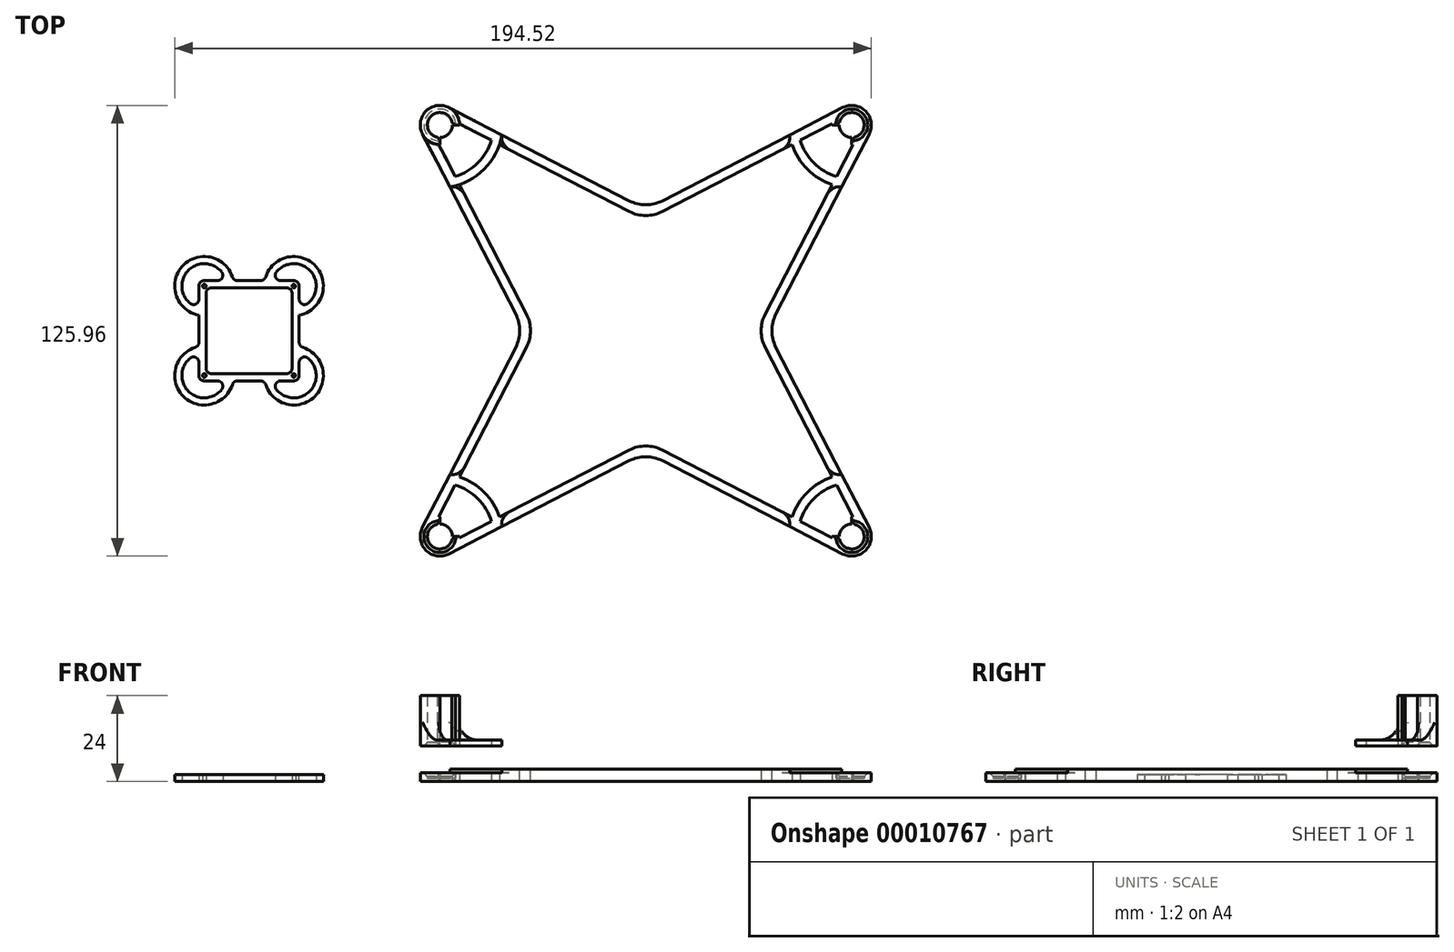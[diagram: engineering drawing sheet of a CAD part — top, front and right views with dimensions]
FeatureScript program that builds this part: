
annotation { "Feature Type Name" : "Feature", "Feature Type Description" : "" }
export const myFeature = defineFeature(function(context is Context, id is Id, definition is map)
    precondition{}
    {
        {
            var Q0;
            Q0=qCreatedBy(makeId("Top.planeOp"),FACE);
            var sketch = newSketch(context, id + "F0", { "sketchPlane" : qUnion([Q0])});
            skLineSegment(sketch, "E0.rect.bottom", {"start": v(57.5, 57.5) * mm, "end": v(-57.5, 57.5) * mm});
            skLineSegment(sketch, "E0.rect.top", {"start": v(57.5, -57.5) * mm, "end": v(-57.5, -57.5) * mm});
            skLineSegment(sketch, "E0.rect.left", {"start": v(57.5, 57.5) * mm, "end": v(57.5, -57.5) * mm});
            skLineSegment(sketch, "E0.rect.right", {"start": v(-57.5, 57.5) * mm, "end": v(-57.5, -57.5) * mm});
            skPoint(sketch, "E0.rect.middle", {"position": v(0, 0) * mm});
            skLineSegment(sketch, "E1", {"start": v(0, 33.94) * mm, "end": v(-33.94, 0) * mm});
            skLineSegment(sketch, "E2", {"start": v(-33.94, 0) * mm, "end": v(0, -33.94) * mm});
            skLineSegment(sketch, "E3", {"start": v(0, -33.94) * mm, "end": v(33.94, 0) * mm});
            skLineSegment(sketch, "E4", {"start": v(33.94, 0) * mm, "end": v(0, 33.94) * mm});
            skCircle(sketch, "E5", {"center": v(57.5, 57.5) * mm, "radius": 3.48 * mm});
            skCircle(sketch, "E6", {"center": v(57.5, 57.5) * mm, "radius": 5.47 * mm});
            skLineSegment(sketch, "E7", {"start": v(57.5, 60.98) * mm, "end": v(57.5, 62.98) * mm, "construction": true});
            skCircle(sketch, "E8", {"center": v(-57.5, 57.5) * mm, "radius": 3.48 * mm});
            skCircle(sketch, "E9", {"center": v(-57.5, 57.5) * mm, "radius": 5.47 * mm});
            skCircle(sketch, "E10", {"center": v(-57.5, -57.5) * mm, "radius": 3.48 * mm});
            skCircle(sketch, "E11", {"center": v(-57.5, -57.5) * mm, "radius": 5.47 * mm});
            skCircle(sketch, "E12", {"center": v(57.5, -57.5) * mm, "radius": 3.48 * mm});
            skCircle(sketch, "E13", {"center": v(57.5, -57.5) * mm, "radius": 5.47 * mm});
            skLineSegment(sketch, "E14", {"start": v(62.36, 54.99) * mm, "end": v(33.94, 0) * mm});
            skLineSegment(sketch, "E15", {"start": v(33.94, 0) * mm, "end": v(62.36, -54.99) * mm});
            skLineSegment(sketch, "E16", {"start": v(54.99, -62.36) * mm, "end": v(0, -33.94) * mm});
            skLineSegment(sketch, "E17", {"start": v(0, -33.94) * mm, "end": v(-54.99, -62.36) * mm});
            skLineSegment(sketch, "E18", {"start": v(-62.36, -54.99) * mm, "end": v(-33.94, 0) * mm});
            skLineSegment(sketch, "E19", {"start": v(-33.94, 0) * mm, "end": v(-62.36, 54.99) * mm});
            skLineSegment(sketch, "E20", {"start": v(-54.99, 62.36) * mm, "end": v(0, 33.94) * mm});
            skLineSegment(sketch, "E21", {"start": v(0, 33.94) * mm, "end": v(54.99, 62.36) * mm});
            skLineSegment(sketch, "E22.0", {"start": v(30.94, 0) * mm, "end": v(0, 30.94) * mm});
            skLineSegment(sketch, "E22.1", {"start": v(0, -30.94) * mm, "end": v(30.94, 0) * mm});
            skLineSegment(sketch, "E22.2", {"start": v(-30.94, 0) * mm, "end": v(0, -30.94) * mm});
            skLineSegment(sketch, "E22.3", {"start": v(0, 30.94) * mm, "end": v(-30.94, 0) * mm});
            skLineSegment(sketch, "E23", {"start": v(-30.94, 0) * mm, "end": v(-57.84, 52.04) * mm});
            skLineSegment(sketch, "E24", {"start": v(-30.94, 0) * mm, "end": v(-57.84, -52.04) * mm});
            skLineSegment(sketch, "E25", {"start": v(30.94, 0) * mm, "end": v(33.94, 0) * mm, "construction": true});
            skLineSegment(sketch, "E26", {"start": v(0, -30.94) * mm, "end": v(-52.04, -57.84) * mm});
            skLineSegment(sketch, "E27", {"start": v(0, -30.94) * mm, "end": v(52.04, -57.84) * mm});
            skLineSegment(sketch, "E28", {"start": v(57.84, -52.04) * mm, "end": v(30.94, 0) * mm});
            skLineSegment(sketch, "E29", {"start": v(30.94, 0) * mm, "end": v(57.84, 52.04) * mm});
            skLineSegment(sketch, "E30", {"start": v(52.04, 57.84) * mm, "end": v(0, 30.94) * mm});
            skLineSegment(sketch, "E31", {"start": v(0, 30.94) * mm, "end": v(-52.04, 57.84) * mm});
            skCircle(sketch, "E32", {"center": v(57.5, 57.5) * mm, "radius": 15 * mm});
            skCircle(sketch, "E33", {"center": v(57.5, 57.5) * mm, "radius": 17.5 * mm});
            skLineSegment(sketch, "E34", {"start": v(57.5, 72.5) * mm, "end": v(57.5, 75) * mm, "construction": true});
            skCircle(sketch, "E35", {"center": v(-57.5, 57.5) * mm, "radius": 15 * mm});
            skCircle(sketch, "E36", {"center": v(-57.5, 57.5) * mm, "radius": 17.5 * mm});
            skCircle(sketch, "E37", {"center": v(-57.5, -57.5) * mm, "radius": 15 * mm});
            skCircle(sketch, "E38", {"center": v(-57.5, -57.5) * mm, "radius": 17.5 * mm});
            skCircle(sketch, "E39", {"center": v(57.5, -57.5) * mm, "radius": 15 * mm});
            skCircle(sketch, "E40", {"center": v(57.5, -57.5) * mm, "radius": 17.5 * mm});
            skLineSegment(sketch, "E41.rect.bottom", {"start": v(-98.29, 12.5) * mm, "end": v(-123.29, 12.5) * mm, "construction": true});
            skLineSegment(sketch, "E41.rect.top", {"start": v(-98.29, -12.5) * mm, "end": v(-123.29, -12.5) * mm, "construction": true});
            skLineSegment(sketch, "E41.rect.left", {"start": v(-98.29, 12.5) * mm, "end": v(-98.29, -12.5) * mm, "construction": true});
            skLineSegment(sketch, "E41.rect.right", {"start": v(-123.29, 12.5) * mm, "end": v(-123.29, -12.5) * mm, "construction": true});
            skPoint(sketch, "E41.rect.middle", {"position": v(-110.79, 0) * mm});
            skCircle(sketch, "E42", {"center": v(-98.29, 12.5) * mm, "radius": 0.5 * mm});
            skCircle(sketch, "E43", {"center": v(-98.29, -12.5) * mm, "radius": 0.5 * mm});
            skCircle(sketch, "E44", {"center": v(-123.29, -12.5) * mm, "radius": 0.5 * mm});
            skCircle(sketch, "E45", {"center": v(-123.29, 12.5) * mm, "radius": 0.5 * mm});
            skCircle(sketch, "E46", {"center": v(-98.29, 12.5) * mm, "radius": 6.25 * mm});
            skCircle(sketch, "E47", {"center": v(-123.29, 12.5) * mm, "radius": 6.25 * mm});
            skCircle(sketch, "E48", {"center": v(-123.29, -12.5) * mm, "radius": 6.25 * mm});
            skCircle(sketch, "E49", {"center": v(-98.29, -12.5) * mm, "radius": 6.25 * mm});
            skCircle(sketch, "E50", {"center": v(-98.29, 12.5) * mm, "radius": 8.25 * mm});
            skLineSegment(sketch, "E51", {"start": v(-98.29, 18.75) * mm, "end": v(-98.29, 20.75) * mm, "construction": true});
            skCircle(sketch, "E52", {"center": v(-123.29, 12.5) * mm, "radius": 8.25 * mm});
            skCircle(sketch, "E53", {"center": v(-123.29, -12.5) * mm, "radius": 8.25 * mm});
            skCircle(sketch, "E54", {"center": v(-98.29, -12.5) * mm, "radius": 8.25 * mm});
            skLineSegment(sketch, "E55.rect.bottom", {"start": v(-96.79, 14) * mm, "end": v(-124.79, 14) * mm});
            skLineSegment(sketch, "E55.rect.top", {"start": v(-96.79, -14) * mm, "end": v(-124.79, -14) * mm});
            skLineSegment(sketch, "E55.rect.left", {"start": v(-96.79, 14) * mm, "end": v(-96.79, -14) * mm});
            skLineSegment(sketch, "E55.rect.right", {"start": v(-124.79, 14) * mm, "end": v(-124.79, -14) * mm});
            skLineSegment(sketch, "E56.rect.bottom", {"start": v(-98.79, 12) * mm, "end": v(-122.79, 12) * mm});
            skLineSegment(sketch, "E56.rect.top", {"start": v(-98.79, -12) * mm, "end": v(-122.79, -12) * mm});
            skLineSegment(sketch, "E56.rect.left", {"start": v(-98.79, 12) * mm, "end": v(-98.79, -12) * mm});
            skLineSegment(sketch, "E56.rect.right", {"start": v(-122.79, 12) * mm, "end": v(-122.79, -12) * mm});
            skLineSegment(sketch, "E57", {"start": v(-110.79, 12.5) * mm, "end": v(-110.79, 14) * mm, "construction": true});
            skLineSegment(sketch, "E58", {"start": v(-110.79, 12.5) * mm, "end": v(-110.79, 12) * mm, "construction": true});
            skCircle(sketch, "E59.cCircle", {"center": v(-110.79, 0) * mm, "radius": 17.68 * mm, "construction": true});
            skLineSegment(sketch, "E59.0", {"start": v(-110.79, 25) * mm, "end": v(-85.79, 0) * mm});
            skLineSegment(sketch, "E59.1", {"start": v(-85.79, 0) * mm, "end": v(-110.79, -25) * mm});
            skLineSegment(sketch, "E59.2", {"start": v(-110.79, -25) * mm, "end": v(-135.79, 0) * mm});
            skLineSegment(sketch, "E59.3", {"start": v(-135.79, 0) * mm, "end": v(-110.79, 25) * mm});
            skLineSegment(sketch, "E60", {"start": v(-124.79, 14) * mm, "end": v(-124.79, 20.61) * mm});
            skLineSegment(sketch, "E61", {"start": v(-122.79, 14) * mm, "end": v(-122.79, 20.73) * mm});
            skLineSegment(sketch, "E62", {"start": v(-98.79, 14) * mm, "end": v(-98.79, 20.73) * mm});
            skLineSegment(sketch, "E63", {"start": v(-96.79, 14) * mm, "end": v(-96.79, 20.61) * mm});
            skLineSegment(sketch, "E64", {"start": v(-124.79, -14) * mm, "end": v(-124.79, -20.61) * mm});
            skLineSegment(sketch, "E65", {"start": v(-122.79, -14) * mm, "end": v(-122.79, -20.73) * mm});
            skLineSegment(sketch, "E66", {"start": v(-98.79, -14) * mm, "end": v(-98.79, -20.73) * mm});
            skLineSegment(sketch, "E67", {"start": v(-96.79, -14) * mm, "end": v(-96.79, -20.61) * mm});
            skSolve(sketch);
        }
        {
            var Q0;
            {var subQ0=sQuery(id+"F0.wireOp",EDGE,"E9");var subQ7=sQuery(id+"F0.wireOp",EDGE,"E0.rect.bottom");var subQ8=makeQuery(id+"F0.imprint","INTERSECT",VERTEX,{"derivedFrom":[subQ7,subQ0]});Q0=makeQuery(id+"F0.imprint","IMPRINT",FACE,{"disambiguationData":[TD([[makeQuery(id+"F0.imprint","IMPRINT",EDGE,{"disambiguationData":[TD([[subQ8,-1.0]])],"derivedFrom":subQ7}),-1.0]])]});}
            var Q1;
            {var subQ1=sQuery(id+"F0.wireOp",EDGE,"E0.rect.right");var subQ5=sQuery(id+"F0.wireOp",EDGE,"E23");var subQ6=makeQuery(id+"F0.imprint","INTERSECT",VERTEX,{"derivedFrom":[subQ1,subQ5]});Q1=makeQuery(id+"F0.imprint","IMPRINT",FACE,{"disambiguationData":[TD([[makeQuery(id+"F0.imprint","IMPRINT",EDGE,{"disambiguationData":[TD([[subQ6,-1.0]])],"derivedFrom":subQ1}),-1.0]])]});}
            var Q2;
            {var subQ1=sQuery(id+"F0.wireOp",EDGE,"E23");var subQ5=sQuery(id+"F0.wireOp",EDGE,"E0.rect.right");var subQ6=makeQuery(id+"F0.imprint","INTERSECT",VERTEX,{"derivedFrom":[subQ5,subQ1]});Q2=makeQuery(id+"F0.imprint","IMPRINT",FACE,{"disambiguationData":[TD([[makeQuery(id+"F0.imprint","IMPRINT",EDGE,{"disambiguationData":[TD([[subQ6,-1.0]])],"derivedFrom":subQ5}),1.0]])]});}
            var Q3;
            {var subQ1=sQuery(id+"F0.wireOp",EDGE,"E0.rect.bottom");var subQ5=sQuery(id+"F0.wireOp",EDGE,"E20");var subQ6=makeQuery(id+"F0.imprint","INTERSECT",VERTEX,{"derivedFrom":[subQ1,subQ5]});Q3=makeQuery(id+"F0.imprint","IMPRINT",FACE,{"disambiguationData":[TD([[makeQuery(id+"F0.imprint","IMPRINT",EDGE,{"disambiguationData":[TD([[subQ6,-1.0]])],"derivedFrom":subQ1}),-1.0]])]});}
            var Q4;
            {var subQ3=sQuery(id+"F0.wireOp",EDGE,"E20");var subQ5=sQuery(id+"F0.wireOp",EDGE,"E0.rect.bottom");var subQ7=makeQuery(id+"F0.imprint","INTERSECT",VERTEX,{"derivedFrom":[subQ5,subQ3]});Q4=makeQuery(id+"F0.imprint","IMPRINT",FACE,{"disambiguationData":[TD([[makeQuery(id+"F0.imprint","IMPRINT",EDGE,{"disambiguationData":[TD([[subQ7,-1.0]])],"derivedFrom":subQ5}),1.0]])]});}
            var Q5;
            {var subQ0=sQuery(id+"F0.wireOp",EDGE,"E36");var subQ3=sQuery(id+"F0.wireOp",EDGE,"E19");var subQ4=makeQuery(id+"F0.imprint","INTERSECT",VERTEX,{"derivedFrom":[subQ3,subQ0]});Q5=makeQuery(id+"F0.imprint","IMPRINT",FACE,{"disambiguationData":[TD([[makeQuery(id+"F0.imprint","IMPRINT",EDGE,{"disambiguationData":[TD([[subQ4,-1.0]])],"derivedFrom":subQ3}),-1.0]])]});}
            var Q6;
            {var subQ3=sQuery(id+"F0.wireOp",EDGE,"E23");var subQ5=sQuery(id+"F0.wireOp",EDGE,"E36");var subQ7=makeQuery(id+"F0.imprint","INTERSECT",VERTEX,{"derivedFrom":[subQ3,subQ5]});Q6=makeQuery(id+"F0.imprint","IMPRINT",FACE,{"disambiguationData":[TD([[makeQuery(id+"F0.imprint","IMPRINT",EDGE,{"disambiguationData":[TD([[subQ7,-1.0]])],"derivedFrom":subQ3}),-1.0]])]});}
            var Q7;
            {var subQ3=sQuery(id+"F0.wireOp",EDGE,"E20");var subQ5=sQuery(id+"F0.wireOp",EDGE,"E35");var subQ7=makeQuery(id+"F0.imprint","INTERSECT",VERTEX,{"derivedFrom":[subQ3,subQ5]});Q7=makeQuery(id+"F0.imprint","IMPRINT",FACE,{"disambiguationData":[TD([[makeQuery(id+"F0.imprint","IMPRINT",EDGE,{"disambiguationData":[TD([[subQ7,-1.0]])],"derivedFrom":subQ3}),-1.0]])]});}
            extrude(context, id + "F1", {"entities" : qUnion([Q0, Q1, Q2, Q3, Q4, Q5, Q6, Q7]), "depth" : 1.6 * mm});
        }
        {
            var Q0;
            {var subQ0=sQuery(id+"F0.wireOp",EDGE,"E9");var subQ7=sQuery(id+"F0.wireOp",EDGE,"E0.rect.bottom");var subQ8=makeQuery(id+"F0.imprint","INTERSECT",VERTEX,{"derivedFrom":[subQ7,subQ0]});Q0=makeQuery(id+"F0.imprint","IMPRINT",FACE,{"disambiguationData":[TD([[makeQuery(id+"F0.imprint","IMPRINT",EDGE,{"disambiguationData":[TD([[subQ8,-1.0]])],"derivedFrom":subQ7}),-1.0]])]});}
            extrude(context, id + "F2", {"entities" : qUnion([Q0]), "operationType" : NewBodyOperationType.ADD, "depth" : 14 * mm});
        }
        {
            var Q0;
            {var subQ0=sQuery(id+"F0.wireOp",EDGE,"E9");Q0=makeQuery(id+"F2.boolean.opBoolean","INTERSECT",EDGE,{"disambiguationData":[OD(0.0)],"derivedFrom":[makeQuery(id+"F1.opExtrude","CAP_FACE",FACE,{"disambiguationData":[OSD([sQuery(id+"F0.wireOp",EDGE,"E0.rect.bottom"),sQuery(id+"F0.wireOp",EDGE,"E0.rect.right"),sQuery(id+"F0.wireOp",EDGE,"E8"),subQ0,sQuery(id+"F0.wireOp",EDGE,"E19"),sQuery(id+"F0.wireOp",EDGE,"E20"),sQuery(id+"F0.wireOp",EDGE,"E23"),sQuery(id+"F0.wireOp",EDGE,"E31"),sQuery(id+"F0.wireOp",EDGE,"E35"),sQuery(id+"F0.wireOp",EDGE,"E36")])],"isStart":false}),makeQuery(id+"F2.opExtrude","SWEPT_FACE",FACE,{"disambiguationData":[OSD([subQ0])]})]});}
            var Q1;
            {var subQ0=sQuery(id+"F0.wireOp",EDGE,"E9");Q1=makeQuery(id+"F2.boolean.opBoolean","INTERSECT",EDGE,{"disambiguationData":[OD(1.0)],"derivedFrom":[makeQuery(id+"F1.opExtrude","CAP_FACE",FACE,{"disambiguationData":[OSD([sQuery(id+"F0.wireOp",EDGE,"E0.rect.bottom"),sQuery(id+"F0.wireOp",EDGE,"E0.rect.right"),sQuery(id+"F0.wireOp",EDGE,"E8"),subQ0,sQuery(id+"F0.wireOp",EDGE,"E19"),sQuery(id+"F0.wireOp",EDGE,"E20"),sQuery(id+"F0.wireOp",EDGE,"E23"),sQuery(id+"F0.wireOp",EDGE,"E31"),sQuery(id+"F0.wireOp",EDGE,"E35"),sQuery(id+"F0.wireOp",EDGE,"E36")])],"isStart":false}),makeQuery(id+"F2.opExtrude","SWEPT_FACE",FACE,{"disambiguationData":[OSD([subQ0])]})]});}
            fillet(context, id + "F3", {"entities" : qUnion([Q0, Q1]), "radius" : 5 * mm, "tangentPropagation" : true, "allowEdgeOverflow" : false});
        }
        {
            var Q0;
            Q0=makeQuery(id+"F1.opExtrude","SWEPT_BODY",BODY,{"disambiguationData":[OSD([sQuery(id+"F0.wireOp",EDGE,"E0.rect.bottom"),sQuery(id+"F0.wireOp",EDGE,"E0.rect.right"),sQuery(id+"F0.wireOp",EDGE,"E8"),sQuery(id+"F0.wireOp",EDGE,"E9"),sQuery(id+"F0.wireOp",EDGE,"E19"),sQuery(id+"F0.wireOp",EDGE,"E20"),sQuery(id+"F0.wireOp",EDGE,"E23"),sQuery(id+"F0.wireOp",EDGE,"E31"),sQuery(id+"F0.wireOp",EDGE,"E35"),sQuery(id+"F0.wireOp",EDGE,"E36")])]});
            transform(context, id + "F4", {"entities" : qUnion([Q0]), "transformType" : TransformType.TRANSLATION_3D, "dx" : 0 * mm, "dy" : 0 * mm, "dz" : 10 * mm, "makeCopy" : false});
        }
        {
            var Q0;
            {var subQ1=sQuery(id+"F0.wireOp",EDGE,"E23");var subQ5=sQuery(id+"F0.wireOp",EDGE,"E0.rect.right");var subQ6=makeQuery(id+"F0.imprint","INTERSECT",VERTEX,{"derivedFrom":[subQ5,subQ1]});Q0=makeQuery(id+"F0.imprint","IMPRINT",FACE,{"disambiguationData":[TD([[makeQuery(id+"F0.imprint","IMPRINT",EDGE,{"disambiguationData":[TD([[subQ6,-1.0]])],"derivedFrom":subQ5}),1.0]])]});}
            var Q1;
            {var subQ1=sQuery(id+"F0.wireOp",EDGE,"E0.rect.right");var subQ5=sQuery(id+"F0.wireOp",EDGE,"E23");var subQ6=makeQuery(id+"F0.imprint","INTERSECT",VERTEX,{"derivedFrom":[subQ1,subQ5]});Q1=makeQuery(id+"F0.imprint","IMPRINT",FACE,{"disambiguationData":[TD([[makeQuery(id+"F0.imprint","IMPRINT",EDGE,{"disambiguationData":[TD([[subQ6,-1.0]])],"derivedFrom":subQ1}),-1.0]])]});}
            var Q2;
            {var subQ0=sQuery(id+"F0.wireOp",EDGE,"E9");var subQ7=sQuery(id+"F0.wireOp",EDGE,"E0.rect.bottom");var subQ8=makeQuery(id+"F0.imprint","INTERSECT",VERTEX,{"derivedFrom":[subQ7,subQ0]});Q2=makeQuery(id+"F0.imprint","IMPRINT",FACE,{"disambiguationData":[TD([[makeQuery(id+"F0.imprint","IMPRINT",EDGE,{"disambiguationData":[TD([[subQ8,-1.0]])],"derivedFrom":subQ7}),-1.0]])]});}
            var Q3;
            {var subQ1=sQuery(id+"F0.wireOp",EDGE,"E0.rect.bottom");var subQ5=sQuery(id+"F0.wireOp",EDGE,"E20");var subQ6=makeQuery(id+"F0.imprint","INTERSECT",VERTEX,{"derivedFrom":[subQ1,subQ5]});Q3=makeQuery(id+"F0.imprint","IMPRINT",FACE,{"disambiguationData":[TD([[makeQuery(id+"F0.imprint","IMPRINT",EDGE,{"disambiguationData":[TD([[subQ6,-1.0]])],"derivedFrom":subQ1}),-1.0]])]});}
            var Q4;
            {var subQ3=sQuery(id+"F0.wireOp",EDGE,"E20");var subQ5=sQuery(id+"F0.wireOp",EDGE,"E0.rect.bottom");var subQ7=makeQuery(id+"F0.imprint","INTERSECT",VERTEX,{"derivedFrom":[subQ5,subQ3]});Q4=makeQuery(id+"F0.imprint","IMPRINT",FACE,{"disambiguationData":[TD([[makeQuery(id+"F0.imprint","IMPRINT",EDGE,{"disambiguationData":[TD([[subQ7,-1.0]])],"derivedFrom":subQ5}),1.0]])]});}
            var Q5;
            {var subQ0=sQuery(id+"F0.wireOp",EDGE,"E36");var subQ3=sQuery(id+"F0.wireOp",EDGE,"E19");var subQ4=makeQuery(id+"F0.imprint","INTERSECT",VERTEX,{"derivedFrom":[subQ3,subQ0]});Q5=makeQuery(id+"F0.imprint","IMPRINT",FACE,{"disambiguationData":[TD([[makeQuery(id+"F0.imprint","IMPRINT",EDGE,{"disambiguationData":[TD([[subQ4,-1.0]])],"derivedFrom":subQ3}),-1.0]])]});}
            var Q6;
            {var subQ3=sQuery(id+"F0.wireOp",EDGE,"E20");var subQ5=sQuery(id+"F0.wireOp",EDGE,"E35");var subQ7=makeQuery(id+"F0.imprint","INTERSECT",VERTEX,{"derivedFrom":[subQ3,subQ5]});Q6=makeQuery(id+"F0.imprint","IMPRINT",FACE,{"disambiguationData":[TD([[makeQuery(id+"F0.imprint","IMPRINT",EDGE,{"disambiguationData":[TD([[subQ7,-1.0]])],"derivedFrom":subQ3}),-1.0]])]});}
            var Q7;
            {var subQ0=sQuery(id+"F0.wireOp",EDGE,"E33");var subQ3=sQuery(id+"F0.wireOp",EDGE,"E21");var subQ4=makeQuery(id+"F0.imprint","INTERSECT",VERTEX,{"derivedFrom":[subQ3,subQ0]});Q7=makeQuery(id+"F0.imprint","IMPRINT",FACE,{"disambiguationData":[TD([[makeQuery(id+"F0.imprint","IMPRINT",EDGE,{"disambiguationData":[TD([[subQ4,-1.0]])],"derivedFrom":subQ3}),-1.0]])]});}
            var Q8;
            {var subQ1=sQuery(id+"F0.wireOp",EDGE,"E30");var subQ5=sQuery(id+"F0.wireOp",EDGE,"E0.rect.bottom");var subQ6=makeQuery(id+"F0.imprint","INTERSECT",VERTEX,{"derivedFrom":[subQ5,subQ1]});Q8=makeQuery(id+"F0.imprint","IMPRINT",FACE,{"disambiguationData":[TD([[makeQuery(id+"F0.imprint","IMPRINT",EDGE,{"disambiguationData":[TD([[subQ6,-1.0]])],"derivedFrom":subQ5}),1.0]])]});}
            var Q9;
            {var subQ0=sQuery(id+"F0.wireOp",EDGE,"E30");var subQ1=sQuery(id+"F0.wireOp",EDGE,"E0.rect.bottom");var subQ2=makeQuery(id+"F0.imprint","INTERSECT",VERTEX,{"derivedFrom":[subQ1,subQ0]});Q9=makeQuery(id+"F0.imprint","IMPRINT",FACE,{"disambiguationData":[TD([[makeQuery(id+"F0.imprint","IMPRINT",EDGE,{"disambiguationData":[TD([[subQ2,-1.0]])],"derivedFrom":subQ1}),-1.0]])]});}
            var Q10;
            {var subQ7=sQuery(id+"F0.wireOp",EDGE,"E5");var subQ9=sQuery(id+"F0.wireOp",EDGE,"E0.rect.bottom");var subQ10=makeQuery(id+"F0.imprint","INTERSECT",VERTEX,{"derivedFrom":[subQ9,subQ7]});Q10=makeQuery(id+"F0.imprint","IMPRINT",FACE,{"disambiguationData":[TD([[makeQuery(id+"F0.imprint","IMPRINT",EDGE,{"disambiguationData":[TD([[subQ10,-1.0]])],"derivedFrom":subQ9}),-1.0]])]});}
            var Q11;
            {var subQ0=sQuery(id+"F0.wireOp",EDGE,"E29");var subQ1=sQuery(id+"F0.wireOp",EDGE,"E0.rect.left");var subQ2=makeQuery(id+"F0.imprint","INTERSECT",VERTEX,{"derivedFrom":[subQ1,subQ0]});Q11=makeQuery(id+"F0.imprint","IMPRINT",FACE,{"disambiguationData":[TD([[makeQuery(id+"F0.imprint","IMPRINT",EDGE,{"disambiguationData":[TD([[subQ2,-1.0]])],"derivedFrom":subQ1}),1.0]])]});}
            var Q12;
            {var subQ1=sQuery(id+"F0.wireOp",EDGE,"E29");var subQ5=sQuery(id+"F0.wireOp",EDGE,"E0.rect.left");var subQ6=makeQuery(id+"F0.imprint","INTERSECT",VERTEX,{"derivedFrom":[subQ5,subQ1]});Q12=makeQuery(id+"F0.imprint","IMPRINT",FACE,{"disambiguationData":[TD([[makeQuery(id+"F0.imprint","IMPRINT",EDGE,{"disambiguationData":[TD([[subQ6,-1.0]])],"derivedFrom":subQ5}),-1.0]])]});}
            var Q13;
            {var subQ3=sQuery(id+"F0.wireOp",EDGE,"E14");var subQ5=sQuery(id+"F0.wireOp",EDGE,"E32");var subQ7=makeQuery(id+"F0.imprint","INTERSECT",VERTEX,{"derivedFrom":[subQ3,subQ5]});Q13=makeQuery(id+"F0.imprint","IMPRINT",FACE,{"disambiguationData":[TD([[makeQuery(id+"F0.imprint","IMPRINT",EDGE,{"disambiguationData":[TD([[subQ7,-1.0]])],"derivedFrom":subQ3}),-1.0]])]});}
            var Q14;
            {var subQ0=sQuery(id+"F0.wireOp",EDGE,"E40");var subQ3=sQuery(id+"F0.wireOp",EDGE,"E15");var subQ4=makeQuery(id+"F0.imprint","INTERSECT",VERTEX,{"derivedFrom":[subQ3,subQ0]});Q14=makeQuery(id+"F0.imprint","IMPRINT",FACE,{"disambiguationData":[TD([[makeQuery(id+"F0.imprint","IMPRINT",EDGE,{"disambiguationData":[TD([[subQ4,-1.0]])],"derivedFrom":subQ3}),-1.0]])]});}
            var Q15;
            {var subQ3=sQuery(id+"F0.wireOp",EDGE,"E18");var subQ5=sQuery(id+"F0.wireOp",EDGE,"E37");var subQ7=makeQuery(id+"F0.imprint","INTERSECT",VERTEX,{"derivedFrom":[subQ3,subQ5]});Q15=makeQuery(id+"F0.imprint","IMPRINT",FACE,{"disambiguationData":[TD([[makeQuery(id+"F0.imprint","IMPRINT",EDGE,{"disambiguationData":[TD([[subQ7,-1.0]])],"derivedFrom":subQ3}),-1.0]])]});}
            var Q16;
            {var subQ3=sQuery(id+"F0.wireOp",EDGE,"E18");var subQ5=sQuery(id+"F0.wireOp",EDGE,"E0.rect.right");var subQ7=makeQuery(id+"F0.imprint","INTERSECT",VERTEX,{"derivedFrom":[subQ5,subQ3]});Q16=makeQuery(id+"F0.imprint","IMPRINT",FACE,{"disambiguationData":[TD([[makeQuery(id+"F0.imprint","IMPRINT",EDGE,{"disambiguationData":[TD([[subQ7,-1.0]])],"derivedFrom":subQ5}),1.0]])]});}
            var Q17;
            {var subQ1=sQuery(id+"F0.wireOp",EDGE,"E0.rect.right");var subQ5=sQuery(id+"F0.wireOp",EDGE,"E18");var subQ6=makeQuery(id+"F0.imprint","INTERSECT",VERTEX,{"derivedFrom":[subQ1,subQ5]});Q17=makeQuery(id+"F0.imprint","IMPRINT",FACE,{"disambiguationData":[TD([[makeQuery(id+"F0.imprint","IMPRINT",EDGE,{"disambiguationData":[TD([[subQ6,-1.0]])],"derivedFrom":subQ1}),-1.0]])]});}
            var Q18;
            {var subQ0=sQuery(id+"F0.wireOp",EDGE,"E11");var subQ1=sQuery(id+"F0.wireOp",EDGE,"E0.rect.top");var subQ2=makeQuery(id+"F0.imprint","INTERSECT",VERTEX,{"derivedFrom":[subQ1,subQ0]});Q18=makeQuery(id+"F0.imprint","IMPRINT",FACE,{"disambiguationData":[TD([[makeQuery(id+"F0.imprint","IMPRINT",EDGE,{"disambiguationData":[TD([[subQ2,-1.0]])],"derivedFrom":subQ1}),1.0]])]});}
            var Q19;
            {var subQ1=sQuery(id+"F0.wireOp",EDGE,"E0.rect.top");var subQ5=sQuery(id+"F0.wireOp",EDGE,"E17");var subQ6=makeQuery(id+"F0.imprint","INTERSECT",VERTEX,{"derivedFrom":[subQ1,subQ5]});Q19=makeQuery(id+"F0.imprint","IMPRINT",FACE,{"disambiguationData":[TD([[makeQuery(id+"F0.imprint","IMPRINT",EDGE,{"disambiguationData":[TD([[subQ6,-1.0]])],"derivedFrom":subQ1}),1.0]])]});}
            var Q20;
            {var subQ3=sQuery(id+"F0.wireOp",EDGE,"E17");var subQ5=sQuery(id+"F0.wireOp",EDGE,"E0.rect.top");var subQ7=makeQuery(id+"F0.imprint","INTERSECT",VERTEX,{"derivedFrom":[subQ5,subQ3]});Q20=makeQuery(id+"F0.imprint","IMPRINT",FACE,{"disambiguationData":[TD([[makeQuery(id+"F0.imprint","IMPRINT",EDGE,{"disambiguationData":[TD([[subQ7,-1.0]])],"derivedFrom":subQ5}),-1.0]])]});}
            var Q21;
            {var subQ0=sQuery(id+"F0.wireOp",EDGE,"E38");var subQ3=sQuery(id+"F0.wireOp",EDGE,"E17");var subQ4=makeQuery(id+"F0.imprint","INTERSECT",VERTEX,{"derivedFrom":[subQ3,subQ0]});Q21=makeQuery(id+"F0.imprint","IMPRINT",FACE,{"disambiguationData":[TD([[makeQuery(id+"F0.imprint","IMPRINT",EDGE,{"disambiguationData":[TD([[subQ4,-1.0]])],"derivedFrom":subQ3}),-1.0]])]});}
            var Q22;
            {var subQ3=sQuery(id+"F0.wireOp",EDGE,"E16");var subQ5=sQuery(id+"F0.wireOp",EDGE,"E39");var subQ7=makeQuery(id+"F0.imprint","INTERSECT",VERTEX,{"derivedFrom":[subQ3,subQ5]});Q22=makeQuery(id+"F0.imprint","IMPRINT",FACE,{"disambiguationData":[TD([[makeQuery(id+"F0.imprint","IMPRINT",EDGE,{"disambiguationData":[TD([[subQ7,-1.0]])],"derivedFrom":subQ3}),-1.0]])]});}
            var Q23;
            {var subQ3=sQuery(id+"F0.wireOp",EDGE,"E0.rect.top");var subQ9=sQuery(id+"F0.wireOp",EDGE,"E12");var subQ11=makeQuery(id+"F0.imprint","INTERSECT",VERTEX,{"derivedFrom":[subQ3,subQ9]});Q23=makeQuery(id+"F0.imprint","IMPRINT",FACE,{"disambiguationData":[TD([[makeQuery(id+"F0.imprint","IMPRINT",EDGE,{"disambiguationData":[TD([[subQ11,-1.0]])],"derivedFrom":subQ3}),1.0]])]});}
            var Q24;
            {var subQ1=sQuery(id+"F0.wireOp",EDGE,"E0.rect.top");var subQ5=sQuery(id+"F0.wireOp",EDGE,"E27");var subQ6=makeQuery(id+"F0.imprint","INTERSECT",VERTEX,{"derivedFrom":[subQ1,subQ5]});Q24=makeQuery(id+"F0.imprint","IMPRINT",FACE,{"disambiguationData":[TD([[makeQuery(id+"F0.imprint","IMPRINT",EDGE,{"disambiguationData":[TD([[subQ6,-1.0]])],"derivedFrom":subQ1}),1.0]])]});}
            var Q25;
            {var subQ1=sQuery(id+"F0.wireOp",EDGE,"E27");var subQ5=sQuery(id+"F0.wireOp",EDGE,"E0.rect.top");var subQ6=makeQuery(id+"F0.imprint","INTERSECT",VERTEX,{"derivedFrom":[subQ5,subQ1]});Q25=makeQuery(id+"F0.imprint","IMPRINT",FACE,{"disambiguationData":[TD([[makeQuery(id+"F0.imprint","IMPRINT",EDGE,{"disambiguationData":[TD([[subQ6,-1.0]])],"derivedFrom":subQ5}),-1.0]])]});}
            var Q26;
            {var subQ1=sQuery(id+"F0.wireOp",EDGE,"E0.rect.left");var subQ5=sQuery(id+"F0.wireOp",EDGE,"E15");var subQ6=makeQuery(id+"F0.imprint","INTERSECT",VERTEX,{"derivedFrom":[subQ1,subQ5]});Q26=makeQuery(id+"F0.imprint","IMPRINT",FACE,{"disambiguationData":[TD([[makeQuery(id+"F0.imprint","IMPRINT",EDGE,{"disambiguationData":[TD([[subQ6,-1.0]])],"derivedFrom":subQ1}),1.0]])]});}
            var Q27;
            {var subQ3=sQuery(id+"F0.wireOp",EDGE,"E15");var subQ5=sQuery(id+"F0.wireOp",EDGE,"E0.rect.left");var subQ7=makeQuery(id+"F0.imprint","INTERSECT",VERTEX,{"derivedFrom":[subQ5,subQ3]});Q27=makeQuery(id+"F0.imprint","IMPRINT",FACE,{"disambiguationData":[TD([[makeQuery(id+"F0.imprint","IMPRINT",EDGE,{"disambiguationData":[TD([[subQ7,-1.0]])],"derivedFrom":subQ5}),-1.0]])]});}
            var Q28;
            {var subQ3=sQuery(id+"F0.wireOp",EDGE,"E23");var subQ5=sQuery(id+"F0.wireOp",EDGE,"E36");var subQ7=makeQuery(id+"F0.imprint","INTERSECT",VERTEX,{"derivedFrom":[subQ3,subQ5]});Q28=makeQuery(id+"F0.imprint","IMPRINT",FACE,{"disambiguationData":[TD([[makeQuery(id+"F0.imprint","IMPRINT",EDGE,{"disambiguationData":[TD([[subQ7,-1.0]])],"derivedFrom":subQ3}),-1.0]])]});}
            var Q29;
            {var subQ0=sQuery(id+"F0.wireOp",EDGE,"E33");var subQ3=sQuery(id+"F0.wireOp",EDGE,"E29");var subQ4=makeQuery(id+"F0.imprint","INTERSECT",VERTEX,{"derivedFrom":[subQ3,subQ0]});Q29=makeQuery(id+"F0.imprint","IMPRINT",FACE,{"disambiguationData":[TD([[makeQuery(id+"F0.imprint","IMPRINT",EDGE,{"disambiguationData":[TD([[subQ4,-1.0]])],"derivedFrom":subQ3}),1.0]])]});}
            var Q30;
            {var subQ0=sQuery(id+"F0.wireOp",EDGE,"E40");var subQ3=sQuery(id+"F0.wireOp",EDGE,"E27");var subQ4=makeQuery(id+"F0.imprint","INTERSECT",VERTEX,{"derivedFrom":[subQ3,subQ0]});Q30=makeQuery(id+"F0.imprint","IMPRINT",FACE,{"disambiguationData":[TD([[makeQuery(id+"F0.imprint","IMPRINT",EDGE,{"disambiguationData":[TD([[subQ4,-1.0]])],"derivedFrom":subQ3}),1.0]])]});}
            var Q31;
            {var subQ0=sQuery(id+"F0.wireOp",EDGE,"E38");var subQ3=sQuery(id+"F0.wireOp",EDGE,"E24");var subQ4=makeQuery(id+"F0.imprint","INTERSECT",VERTEX,{"derivedFrom":[subQ3,subQ0]});Q31=makeQuery(id+"F0.imprint","IMPRINT",FACE,{"disambiguationData":[TD([[makeQuery(id+"F0.imprint","IMPRINT",EDGE,{"disambiguationData":[TD([[subQ4,-1.0]])],"derivedFrom":subQ3}),1.0]])]});}
            extrude(context, id + "F5", {"entities" : qUnion([Q0, Q1, Q2, Q3, Q4, Q5, Q6, Q7, Q8, Q9, Q10, Q11, Q12, Q13, Q14, Q15, Q16, Q17, Q18, Q19, Q20, Q21, Q22, Q23, Q24, Q25, Q26, Q27, Q28, Q29, Q30, Q31]), "depth" : 2.5 * mm});
        }
        {
            var Q0;
            {var subQ1=sQuery(id+"F0.wireOp",EDGE,"E0.rect.right");var subQ3=sQuery(id+"F0.wireOp",EDGE,"E0.rect.bottom");var subQ5=makeQuery(id+"F0.imprint","INTERSECT",VERTEX,{"derivedFrom":[subQ3,subQ1]});Q0=makeQuery(id+"F0.imprint","IMPRINT",FACE,{"disambiguationData":[TD([[makeQuery(id+"F0.imprint","IMPRINT",EDGE,{"disambiguationData":[TD([[subQ5,1.0]])],"derivedFrom":subQ3}),-1.0]])]});}
            var Q1;
            {var subQ1=sQuery(id+"F0.wireOp",EDGE,"E0.rect.right");var subQ3=sQuery(id+"F0.wireOp",EDGE,"E0.rect.bottom");var subQ5=makeQuery(id+"F0.imprint","INTERSECT",VERTEX,{"derivedFrom":[subQ3,subQ1]});Q1=makeQuery(id+"F0.imprint","IMPRINT",FACE,{"disambiguationData":[TD([[makeQuery(id+"F0.imprint","IMPRINT",EDGE,{"disambiguationData":[TD([[subQ5,1.0]])],"derivedFrom":subQ3}),1.0]])]});}
            var Q2;
            {var subQ1=sQuery(id+"F0.wireOp",EDGE,"E0.rect.right");var subQ3=sQuery(id+"F0.wireOp",EDGE,"E0.rect.top");var subQ5=makeQuery(id+"F0.imprint","INTERSECT",VERTEX,{"derivedFrom":[subQ3,subQ1]});Q2=makeQuery(id+"F0.imprint","IMPRINT",FACE,{"disambiguationData":[TD([[makeQuery(id+"F0.imprint","IMPRINT",EDGE,{"disambiguationData":[TD([[subQ5,1.0]])],"derivedFrom":subQ3}),1.0]])]});}
            var Q3;
            {var subQ1=sQuery(id+"F0.wireOp",EDGE,"E0.rect.right");var subQ3=sQuery(id+"F0.wireOp",EDGE,"E0.rect.top");var subQ5=makeQuery(id+"F0.imprint","INTERSECT",VERTEX,{"derivedFrom":[subQ3,subQ1]});Q3=makeQuery(id+"F0.imprint","IMPRINT",FACE,{"disambiguationData":[TD([[makeQuery(id+"F0.imprint","IMPRINT",EDGE,{"disambiguationData":[TD([[subQ5,1.0]])],"derivedFrom":subQ3}),-1.0]])]});}
            var Q4;
            {var subQ1=sQuery(id+"F0.wireOp",EDGE,"E0.rect.left");var subQ3=sQuery(id+"F0.wireOp",EDGE,"E0.rect.top");var subQ5=makeQuery(id+"F0.imprint","INTERSECT",VERTEX,{"derivedFrom":[subQ3,subQ1]});Q4=makeQuery(id+"F0.imprint","IMPRINT",FACE,{"disambiguationData":[TD([[makeQuery(id+"F0.imprint","IMPRINT",EDGE,{"disambiguationData":[TD([[subQ5,-1.0]])],"derivedFrom":subQ3}),1.0]])]});}
            var Q5;
            {var subQ1=sQuery(id+"F0.wireOp",EDGE,"E0.rect.left");var subQ3=sQuery(id+"F0.wireOp",EDGE,"E0.rect.top");var subQ5=makeQuery(id+"F0.imprint","INTERSECT",VERTEX,{"derivedFrom":[subQ3,subQ1]});Q5=makeQuery(id+"F0.imprint","IMPRINT",FACE,{"disambiguationData":[TD([[makeQuery(id+"F0.imprint","IMPRINT",EDGE,{"disambiguationData":[TD([[subQ5,-1.0]])],"derivedFrom":subQ3}),-1.0]])]});}
            var Q6;
            {var subQ1=sQuery(id+"F0.wireOp",EDGE,"E0.rect.left");var subQ3=sQuery(id+"F0.wireOp",EDGE,"E0.rect.bottom");var subQ5=makeQuery(id+"F0.imprint","INTERSECT",VERTEX,{"derivedFrom":[subQ3,subQ1]});Q6=makeQuery(id+"F0.imprint","IMPRINT",FACE,{"disambiguationData":[TD([[makeQuery(id+"F0.imprint","IMPRINT",EDGE,{"disambiguationData":[TD([[subQ5,-1.0]])],"derivedFrom":subQ3}),-1.0]])]});}
            var Q7;
            {var subQ1=sQuery(id+"F0.wireOp",EDGE,"E0.rect.left");var subQ3=sQuery(id+"F0.wireOp",EDGE,"E0.rect.bottom");var subQ5=makeQuery(id+"F0.imprint","INTERSECT",VERTEX,{"derivedFrom":[subQ3,subQ1]});Q7=makeQuery(id+"F0.imprint","IMPRINT",FACE,{"disambiguationData":[TD([[makeQuery(id+"F0.imprint","IMPRINT",EDGE,{"disambiguationData":[TD([[subQ5,-1.0]])],"derivedFrom":subQ3}),1.0]])]});}
            extrude(context, id + "F6", {"entities" : qUnion([Q0, Q1, Q2, Q3, Q4, Q5, Q6, Q7]), "operationType" : NewBodyOperationType.ADD, "depth" : 1 * mm});
        }
        {
            var Q0;
            {var subQ0=sQuery(id+"F0.wireOp",EDGE,"E0.rect.right");var subQ1=sQuery(id+"F0.wireOp",EDGE,"E8");Q0=makeQuery(id+"F2.boolean.opBoolean","MERGE",EDGE,{"derivedFrom":[makeQuery(id+"F1.opExtrude","SWEPT_EDGE",EDGE,{"disambiguationData":[OSD([subQ0,subQ1])]}),makeQuery(id+"F2.opExtrude","SWEPT_EDGE",EDGE,{"disambiguationData":[OSD([subQ0,subQ1])]})]});}
            var Q1;
            {var subQ0=sQuery(id+"F0.wireOp",EDGE,"E0.rect.bottom");var subQ1=sQuery(id+"F0.wireOp",EDGE,"E8");Q1=makeQuery(id+"F2.boolean.opBoolean","MERGE",EDGE,{"derivedFrom":[makeQuery(id+"F1.opExtrude","SWEPT_EDGE",EDGE,{"disambiguationData":[OSD([subQ0,subQ1])]}),makeQuery(id+"F2.opExtrude","SWEPT_EDGE",EDGE,{"disambiguationData":[OSD([subQ0,subQ1])]})]});}
            var Q2;
            {var subQ0=sQuery(id+"F0.wireOp",EDGE,"E0.rect.right");var subQ1=sQuery(id+"F0.wireOp",EDGE,"E8");var subQ2=sQuery(id+"F0.wireOp",EDGE,"E9");Q2=makeQuery(id+"F6.boolean.opBoolean","SPLIT",EDGE,{"disambiguationData":[TD([makeQuery(id+"F5.opExtrude","CAP_FACE",FACE,{"disambiguationData":[OSD([sQuery(id+"F0.wireOp",EDGE,"E0.rect.bottom"),subQ0,subQ1,subQ2,sQuery(id+"F0.wireOp",EDGE,"E19"),sQuery(id+"F0.wireOp",EDGE,"E20"),sQuery(id+"F0.wireOp",EDGE,"E23"),sQuery(id+"F0.wireOp",EDGE,"E31"),sQuery(id+"F0.wireOp",EDGE,"E35"),sQuery(id+"F0.wireOp",EDGE,"E36")])],"isStart":false})])],"derivedFrom":makeQuery(id+"F5.opExtrude","SWEPT_EDGE",EDGE,{"disambiguationData":[OSD([subQ0,subQ1])]})});}
            var Q3;
            {var subQ0=sQuery(id+"F0.wireOp",EDGE,"E0.rect.bottom");var subQ1=sQuery(id+"F0.wireOp",EDGE,"E8");var subQ2=sQuery(id+"F0.wireOp",EDGE,"E9");Q3=makeQuery(id+"F6.boolean.opBoolean","SPLIT",EDGE,{"disambiguationData":[TD([makeQuery(id+"F5.opExtrude","CAP_FACE",FACE,{"disambiguationData":[OSD([subQ0,sQuery(id+"F0.wireOp",EDGE,"E0.rect.right"),subQ1,subQ2,sQuery(id+"F0.wireOp",EDGE,"E19"),sQuery(id+"F0.wireOp",EDGE,"E20"),sQuery(id+"F0.wireOp",EDGE,"E23"),sQuery(id+"F0.wireOp",EDGE,"E31"),sQuery(id+"F0.wireOp",EDGE,"E35"),sQuery(id+"F0.wireOp",EDGE,"E36")])],"isStart":false})])],"derivedFrom":makeQuery(id+"F5.opExtrude","SWEPT_EDGE",EDGE,{"disambiguationData":[OSD([subQ0,subQ1])]})});}
            var Q4;
            Q4=makeQuery(id+"F1.opExtrude","CAP_EDGE",EDGE,{"disambiguationData":[OSD([sQuery(id+"F0.wireOp",EDGE,"E8")])],"isStart":true});
            var Q5;
            Q5=makeQuery(id+"F5.opExtrude","CAP_EDGE",EDGE,{"disambiguationData":[OSD([sQuery(id+"F0.wireOp",EDGE,"E8")])],"isStart":false});
            var Q6;
            {var subQ0=sQuery(id+"F0.wireOp",EDGE,"E0.rect.right");var subQ1=sQuery(id+"F0.wireOp",EDGE,"E10");var subQ2=sQuery(id+"F0.wireOp",EDGE,"E11");Q6=makeQuery(id+"F6.boolean.opBoolean","SPLIT",EDGE,{"disambiguationData":[TD([makeQuery(id+"F5.opExtrude","CAP_FACE",FACE,{"disambiguationData":[OSD([sQuery(id+"F0.wireOp",EDGE,"E0.rect.top"),subQ0,subQ1,subQ2,sQuery(id+"F0.wireOp",EDGE,"E17"),sQuery(id+"F0.wireOp",EDGE,"E18"),sQuery(id+"F0.wireOp",EDGE,"E24"),sQuery(id+"F0.wireOp",EDGE,"E26"),sQuery(id+"F0.wireOp",EDGE,"E37"),sQuery(id+"F0.wireOp",EDGE,"E38")])],"isStart":false})])],"derivedFrom":makeQuery(id+"F5.opExtrude","SWEPT_EDGE",EDGE,{"disambiguationData":[OSD([subQ0,subQ1])]})});}
            var Q7;
            {var subQ0=sQuery(id+"F0.wireOp",EDGE,"E0.rect.top");var subQ1=sQuery(id+"F0.wireOp",EDGE,"E10");var subQ2=sQuery(id+"F0.wireOp",EDGE,"E11");Q7=makeQuery(id+"F6.boolean.opBoolean","SPLIT",EDGE,{"disambiguationData":[TD([makeQuery(id+"F5.opExtrude","CAP_FACE",FACE,{"disambiguationData":[OSD([subQ0,sQuery(id+"F0.wireOp",EDGE,"E0.rect.right"),subQ1,subQ2,sQuery(id+"F0.wireOp",EDGE,"E17"),sQuery(id+"F0.wireOp",EDGE,"E18"),sQuery(id+"F0.wireOp",EDGE,"E24"),sQuery(id+"F0.wireOp",EDGE,"E26"),sQuery(id+"F0.wireOp",EDGE,"E37"),sQuery(id+"F0.wireOp",EDGE,"E38")])],"isStart":false})])],"derivedFrom":makeQuery(id+"F5.opExtrude","SWEPT_EDGE",EDGE,{"disambiguationData":[OSD([subQ0,subQ1])]})});}
            var Q8;
            Q8=makeQuery(id+"F5.opExtrude","CAP_EDGE",EDGE,{"disambiguationData":[OSD([sQuery(id+"F0.wireOp",EDGE,"E10")])],"isStart":false});
            var Q9;
            {var subQ0=sQuery(id+"F0.wireOp",EDGE,"E0.rect.top");var subQ1=sQuery(id+"F0.wireOp",EDGE,"E12");var subQ2=sQuery(id+"F0.wireOp",EDGE,"E13");Q9=makeQuery(id+"F6.boolean.opBoolean","SPLIT",EDGE,{"disambiguationData":[TD([makeQuery(id+"F5.opExtrude","CAP_FACE",FACE,{"disambiguationData":[OSD([subQ0,sQuery(id+"F0.wireOp",EDGE,"E0.rect.left"),subQ1,subQ2,sQuery(id+"F0.wireOp",EDGE,"E15"),sQuery(id+"F0.wireOp",EDGE,"E16"),sQuery(id+"F0.wireOp",EDGE,"E27"),sQuery(id+"F0.wireOp",EDGE,"E28"),sQuery(id+"F0.wireOp",EDGE,"E39"),sQuery(id+"F0.wireOp",EDGE,"E40")])],"isStart":false})])],"derivedFrom":makeQuery(id+"F5.opExtrude","SWEPT_EDGE",EDGE,{"disambiguationData":[OSD([subQ0,subQ1])]})});}
            var Q10;
            {var subQ0=sQuery(id+"F0.wireOp",EDGE,"E0.rect.left");var subQ1=sQuery(id+"F0.wireOp",EDGE,"E12");var subQ2=sQuery(id+"F0.wireOp",EDGE,"E13");Q10=makeQuery(id+"F6.boolean.opBoolean","SPLIT",EDGE,{"disambiguationData":[TD([makeQuery(id+"F5.opExtrude","CAP_FACE",FACE,{"disambiguationData":[OSD([sQuery(id+"F0.wireOp",EDGE,"E0.rect.top"),subQ0,subQ1,subQ2,sQuery(id+"F0.wireOp",EDGE,"E15"),sQuery(id+"F0.wireOp",EDGE,"E16"),sQuery(id+"F0.wireOp",EDGE,"E27"),sQuery(id+"F0.wireOp",EDGE,"E28"),sQuery(id+"F0.wireOp",EDGE,"E39"),sQuery(id+"F0.wireOp",EDGE,"E40")])],"isStart":false})])],"derivedFrom":makeQuery(id+"F5.opExtrude","SWEPT_EDGE",EDGE,{"disambiguationData":[OSD([subQ0,subQ1])]})});}
            var Q11;
            Q11=makeQuery(id+"F5.opExtrude","CAP_EDGE",EDGE,{"disambiguationData":[OSD([sQuery(id+"F0.wireOp",EDGE,"E12")])],"isStart":false});
            var Q12;
            {var subQ0=sQuery(id+"F0.wireOp",EDGE,"E0.rect.bottom");var subQ1=sQuery(id+"F0.wireOp",EDGE,"E5");var subQ2=sQuery(id+"F0.wireOp",EDGE,"E6");Q12=makeQuery(id+"F6.boolean.opBoolean","SPLIT",EDGE,{"disambiguationData":[TD([makeQuery(id+"F5.opExtrude","CAP_FACE",FACE,{"disambiguationData":[OSD([subQ0,sQuery(id+"F0.wireOp",EDGE,"E0.rect.left"),subQ1,subQ2,sQuery(id+"F0.wireOp",EDGE,"E14"),sQuery(id+"F0.wireOp",EDGE,"E21"),sQuery(id+"F0.wireOp",EDGE,"E29"),sQuery(id+"F0.wireOp",EDGE,"E30"),sQuery(id+"F0.wireOp",EDGE,"E32"),sQuery(id+"F0.wireOp",EDGE,"E33")])],"isStart":false})])],"derivedFrom":makeQuery(id+"F5.opExtrude","SWEPT_EDGE",EDGE,{"disambiguationData":[OSD([subQ0,subQ1])]})});}
            var Q13;
            Q13=makeQuery(id+"F5.opExtrude","CAP_EDGE",EDGE,{"disambiguationData":[OSD([sQuery(id+"F0.wireOp",EDGE,"E5")])],"isStart":false});
            var Q14;
            {var subQ0=sQuery(id+"F0.wireOp",EDGE,"E0.rect.left");var subQ1=sQuery(id+"F0.wireOp",EDGE,"E5");var subQ2=sQuery(id+"F0.wireOp",EDGE,"E6");Q14=makeQuery(id+"F6.boolean.opBoolean","SPLIT",EDGE,{"disambiguationData":[TD([makeQuery(id+"F5.opExtrude","CAP_FACE",FACE,{"disambiguationData":[OSD([sQuery(id+"F0.wireOp",EDGE,"E0.rect.bottom"),subQ0,subQ1,subQ2,sQuery(id+"F0.wireOp",EDGE,"E14"),sQuery(id+"F0.wireOp",EDGE,"E21"),sQuery(id+"F0.wireOp",EDGE,"E29"),sQuery(id+"F0.wireOp",EDGE,"E30"),sQuery(id+"F0.wireOp",EDGE,"E32"),sQuery(id+"F0.wireOp",EDGE,"E33")])],"isStart":false})])],"derivedFrom":makeQuery(id+"F5.opExtrude","SWEPT_EDGE",EDGE,{"disambiguationData":[OSD([subQ0,subQ1])]})});}
            chamfer(context, id + "F7", {"entities" : qUnion([Q0, Q1, Q2, Q3, Q4, Q5, Q6, Q7, Q8, Q9, Q10, Q11, Q12, Q13, Q14]), "width" : 1 * mm, "tangentPropagation" : true});
        }
        {
            var Q0;
            {var subQ1=sQuery(id+"F0.wireOp",EDGE,"E23");var subQ5=sQuery(id+"F0.wireOp",EDGE,"E1");var subQ6=makeQuery(id+"F0.imprint","INTERSECT",VERTEX,{"derivedFrom":[subQ5,subQ1]});Q0=makeQuery(id+"F0.imprint","IMPRINT",FACE,{"disambiguationData":[TD([[makeQuery(id+"F0.imprint","IMPRINT",EDGE,{"disambiguationData":[TD([[subQ6,-1.0]])],"derivedFrom":subQ1}),1.0]])]});}
            var Q1;
            {var subQ1=sQuery(id+"F0.wireOp",EDGE,"E31");var subQ5=sQuery(id+"F0.wireOp",EDGE,"E1");var subQ6=makeQuery(id+"F0.imprint","INTERSECT",VERTEX,{"derivedFrom":[subQ5,subQ1]});Q1=makeQuery(id+"F0.imprint","IMPRINT",FACE,{"disambiguationData":[TD([[makeQuery(id+"F0.imprint","IMPRINT",EDGE,{"disambiguationData":[TD([[subQ6,-1.0]])],"derivedFrom":subQ1}),-1.0]])]});}
            var Q2;
            {var subQ0=sQuery(id+"F0.wireOp",EDGE,"E31");var subQ1=sQuery(id+"F0.wireOp",EDGE,"E1");var subQ2=makeQuery(id+"F0.imprint","INTERSECT",VERTEX,{"derivedFrom":[subQ1,subQ0]});Q2=makeQuery(id+"F0.imprint","IMPRINT",FACE,{"disambiguationData":[TD([[makeQuery(id+"F0.imprint","IMPRINT",EDGE,{"disambiguationData":[TD([[subQ2,1.0]])],"derivedFrom":subQ1}),1.0]])]});}
            var Q3;
            {var subQ1=sQuery(id+"F0.wireOp",EDGE,"E30");var subQ5=sQuery(id+"F0.wireOp",EDGE,"E4");var subQ6=makeQuery(id+"F0.imprint","INTERSECT",VERTEX,{"derivedFrom":[subQ5,subQ1]});Q3=makeQuery(id+"F0.imprint","IMPRINT",FACE,{"disambiguationData":[TD([[makeQuery(id+"F0.imprint","IMPRINT",EDGE,{"disambiguationData":[TD([[subQ6,1.0]])],"derivedFrom":subQ1}),-1.0]])]});}
            var Q4;
            {var subQ1=sQuery(id+"F0.wireOp",EDGE,"E29");var subQ5=sQuery(id+"F0.wireOp",EDGE,"E4");var subQ6=makeQuery(id+"F0.imprint","INTERSECT",VERTEX,{"derivedFrom":[subQ5,subQ1]});Q4=makeQuery(id+"F0.imprint","IMPRINT",FACE,{"disambiguationData":[TD([[makeQuery(id+"F0.imprint","IMPRINT",EDGE,{"disambiguationData":[TD([[subQ6,-1.0]])],"derivedFrom":subQ1}),-1.0]])]});}
            var Q5;
            {var subQ1=sQuery(id+"F0.wireOp",EDGE,"E28");var subQ5=sQuery(id+"F0.wireOp",EDGE,"E3");var subQ6=makeQuery(id+"F0.imprint","INTERSECT",VERTEX,{"derivedFrom":[subQ5,subQ1]});Q5=makeQuery(id+"F0.imprint","IMPRINT",FACE,{"disambiguationData":[TD([[makeQuery(id+"F0.imprint","IMPRINT",EDGE,{"disambiguationData":[TD([[subQ6,1.0]])],"derivedFrom":subQ1}),-1.0]])]});}
            var Q6;
            {var subQ3=sQuery(id+"F0.wireOp",EDGE,"E28");var subQ5=sQuery(id+"F0.wireOp",EDGE,"E3");var subQ6=makeQuery(id+"F0.imprint","INTERSECT",VERTEX,{"derivedFrom":[subQ5,subQ3]});Q6=makeQuery(id+"F0.imprint","IMPRINT",FACE,{"disambiguationData":[TD([[makeQuery(id+"F0.imprint","IMPRINT",EDGE,{"disambiguationData":[TD([[subQ6,-1.0]])],"derivedFrom":subQ5}),1.0]])]});}
            var Q7;
            {var subQ3=sQuery(id+"F0.wireOp",EDGE,"E23");var subQ5=sQuery(id+"F0.wireOp",EDGE,"E1");var subQ6=makeQuery(id+"F0.imprint","INTERSECT",VERTEX,{"derivedFrom":[subQ5,subQ3]});Q7=makeQuery(id+"F0.imprint","IMPRINT",FACE,{"disambiguationData":[TD([[makeQuery(id+"F0.imprint","IMPRINT",EDGE,{"disambiguationData":[TD([[subQ6,-1.0]])],"derivedFrom":subQ5}),1.0]])]});}
            var Q8;
            {var subQ1=sQuery(id+"F0.wireOp",EDGE,"E24");var subQ5=sQuery(id+"F0.wireOp",EDGE,"E2");var subQ6=makeQuery(id+"F0.imprint","INTERSECT",VERTEX,{"derivedFrom":[subQ5,subQ1]});Q8=makeQuery(id+"F0.imprint","IMPRINT",FACE,{"disambiguationData":[TD([[makeQuery(id+"F0.imprint","IMPRINT",EDGE,{"disambiguationData":[TD([[subQ6,-1.0]])],"derivedFrom":subQ1}),-1.0]])]});}
            var Q9;
            {var subQ1=sQuery(id+"F0.wireOp",EDGE,"E26");var subQ5=sQuery(id+"F0.wireOp",EDGE,"E2");var subQ6=makeQuery(id+"F0.imprint","INTERSECT",VERTEX,{"derivedFrom":[subQ5,subQ1]});Q9=makeQuery(id+"F0.imprint","IMPRINT",FACE,{"disambiguationData":[TD([[makeQuery(id+"F0.imprint","IMPRINT",EDGE,{"disambiguationData":[TD([[subQ6,-1.0]])],"derivedFrom":subQ1}),1.0]])]});}
            var Q10;
            {var subQ3=sQuery(id+"F0.wireOp",EDGE,"E26");var subQ5=sQuery(id+"F0.wireOp",EDGE,"E2");var subQ6=makeQuery(id+"F0.imprint","INTERSECT",VERTEX,{"derivedFrom":[subQ5,subQ3]});Q10=makeQuery(id+"F0.imprint","IMPRINT",FACE,{"disambiguationData":[TD([[makeQuery(id+"F0.imprint","IMPRINT",EDGE,{"disambiguationData":[TD([[subQ6,-1.0]])],"derivedFrom":subQ5}),1.0]])]});}
            var Q11;
            {var subQ1=sQuery(id+"F0.wireOp",EDGE,"E27");var subQ5=sQuery(id+"F0.wireOp",EDGE,"E3");var subQ6=makeQuery(id+"F0.imprint","INTERSECT",VERTEX,{"derivedFrom":[subQ5,subQ1]});Q11=makeQuery(id+"F0.imprint","IMPRINT",FACE,{"disambiguationData":[TD([[makeQuery(id+"F0.imprint","IMPRINT",EDGE,{"disambiguationData":[TD([[subQ6,-1.0]])],"derivedFrom":subQ1}),-1.0]])]});}
            extrude(context, id + "F8", {"entities" : qUnion([Q0, Q1, Q2, Q3, Q4, Q5, Q6, Q7, Q8, Q9, Q10, Q11]), "operationType" : NewBodyOperationType.ADD, "depth" : 3.5 * mm});
        }
        {
            var Q0;
            Q0=makeQuery(id+"F8.opExtrude","SWEPT_EDGE",EDGE,{"disambiguationData":[OSD([sQuery(id+"F0.wireOp",EDGE,"E1"),sQuery(id+"F0.wireOp",EDGE,"E2"),sQuery(id+"F0.wireOp",EDGE,"E18"),sQuery(id+"F0.wireOp",EDGE,"E19")])]});
            var Q1;
            Q1=makeQuery(id+"F8.opExtrude","SWEPT_EDGE",EDGE,{"disambiguationData":[OSD([sQuery(id+"F0.wireOp",EDGE,"E22.2"),sQuery(id+"F0.wireOp",EDGE,"E22.3"),sQuery(id+"F0.wireOp",EDGE,"E23"),sQuery(id+"F0.wireOp",EDGE,"E24")])]});
            var Q2;
            Q2=makeQuery(id+"F8.opExtrude","SWEPT_EDGE",EDGE,{"disambiguationData":[OSD([sQuery(id+"F0.wireOp",EDGE,"E2"),sQuery(id+"F0.wireOp",EDGE,"E3"),sQuery(id+"F0.wireOp",EDGE,"E16"),sQuery(id+"F0.wireOp",EDGE,"E17")])]});
            var Q3;
            Q3=makeQuery(id+"F8.opExtrude","SWEPT_EDGE",EDGE,{"disambiguationData":[OSD([sQuery(id+"F0.wireOp",EDGE,"E22.0"),sQuery(id+"F0.wireOp",EDGE,"E22.3"),sQuery(id+"F0.wireOp",EDGE,"E30"),sQuery(id+"F0.wireOp",EDGE,"E31")])]});
            var Q4;
            Q4=makeQuery(id+"F8.opExtrude","SWEPT_EDGE",EDGE,{"disambiguationData":[OSD([sQuery(id+"F0.wireOp",EDGE,"E3"),sQuery(id+"F0.wireOp",EDGE,"E4"),sQuery(id+"F0.wireOp",EDGE,"E14"),sQuery(id+"F0.wireOp",EDGE,"E15")])]});
            var Q5;
            Q5=makeQuery(id+"F8.opExtrude","SWEPT_EDGE",EDGE,{"disambiguationData":[OSD([sQuery(id+"F0.wireOp",EDGE,"E22.1"),sQuery(id+"F0.wireOp",EDGE,"E22.2"),sQuery(id+"F0.wireOp",EDGE,"E26"),sQuery(id+"F0.wireOp",EDGE,"E27")])]});
            var Q6;
            Q6=makeQuery(id+"F8.opExtrude","SWEPT_EDGE",EDGE,{"disambiguationData":[OSD([sQuery(id+"F0.wireOp",EDGE,"E22.0"),sQuery(id+"F0.wireOp",EDGE,"E22.1"),sQuery(id+"F0.wireOp",EDGE,"E28"),sQuery(id+"F0.wireOp",EDGE,"E29")])]});
            var Q7;
            Q7=makeQuery(id+"F8.opExtrude","SWEPT_EDGE",EDGE,{"disambiguationData":[OSD([sQuery(id+"F0.wireOp",EDGE,"E1"),sQuery(id+"F0.wireOp",EDGE,"E4"),sQuery(id+"F0.wireOp",EDGE,"E20"),sQuery(id+"F0.wireOp",EDGE,"E21")])]});
            fillet(context, id + "F9", {"entities" : qUnion([Q0, Q1, Q2, Q3, Q4, Q5, Q6, Q7]), "radius" : 10 * mm, "tangentPropagation" : true, "allowEdgeOverflow" : false});
        }
        {
            var Q0;
            {var subQ1=sQuery(id+"F0.wireOp",EDGE,"E48");var subQ5=sQuery(id+"F0.wireOp",EDGE,"E64");var subQ6=makeQuery(id+"F0.imprint","INTERSECT",VERTEX,{"derivedFrom":[subQ1,subQ5]});Q0=makeQuery(id+"F0.imprint","IMPRINT",FACE,{"disambiguationData":[TD([[makeQuery(id+"F0.imprint","IMPRINT",EDGE,{"disambiguationData":[TD([[subQ6,-1.0]])],"derivedFrom":subQ1}),-1.0]])]});}
            var Q1;
            {var subQ0=sQuery(id+"F0.wireOp",EDGE,"E56.rect.right");var subQ3=sQuery(id+"F0.wireOp",EDGE,"E48");var subQ4=makeQuery(id+"F0.imprint","INTERSECT",VERTEX,{"derivedFrom":[subQ3,subQ0]});Q1=makeQuery(id+"F0.imprint","IMPRINT",FACE,{"disambiguationData":[TD([[makeQuery(id+"F0.imprint","IMPRINT",EDGE,{"disambiguationData":[TD([[subQ4,-1.0]])],"derivedFrom":subQ3}),-1.0]])]});}
            var Q2;
            {var subQ0=sQuery(id+"F0.wireOp",EDGE,"E56.rect.top");var subQ3=sQuery(id+"F0.wireOp",EDGE,"E48");var subQ4=makeQuery(id+"F0.imprint","INTERSECT",VERTEX,{"derivedFrom":[subQ3,subQ0]});Q2=makeQuery(id+"F0.imprint","IMPRINT",FACE,{"disambiguationData":[TD([[makeQuery(id+"F0.imprint","IMPRINT",EDGE,{"disambiguationData":[TD([[subQ4,1.0]])],"derivedFrom":subQ3}),-1.0]])]});}
            var Q3;
            {var subQ3=sQuery(id+"F0.wireOp",EDGE,"E47");var subQ5=sQuery(id+"F0.wireOp",EDGE,"E55.rect.bottom");var subQ7=makeQuery(id+"F0.imprint","INTERSECT",VERTEX,{"derivedFrom":[subQ3,subQ5]});Q3=makeQuery(id+"F0.imprint","IMPRINT",FACE,{"disambiguationData":[TD([[makeQuery(id+"F0.imprint","IMPRINT",EDGE,{"disambiguationData":[TD([[subQ7,1.0]])],"derivedFrom":subQ3}),-1.0]])]});}
            var Q4;
            {var subQ0=sQuery(id+"F0.wireOp",EDGE,"E59.3");var subQ3=sQuery(id+"F0.wireOp",EDGE,"E45");var subQ7=makeQuery(id+"F0.imprint","INTERSECT",VERTEX,{"disambiguationData":[OD(0.0)],"derivedFrom":[subQ3,subQ0]});Q4=makeQuery(id+"F0.imprint","IMPRINT",FACE,{"disambiguationData":[TD([[makeQuery(id+"F0.imprint","IMPRINT",EDGE,{"disambiguationData":[TD([[subQ7,-1.0]])],"derivedFrom":subQ3}),-1.0]])]});}
            var Q5;
            {var subQ0=sQuery(id+"F0.wireOp",EDGE,"E59.3");var subQ3=sQuery(id+"F0.wireOp",EDGE,"E45");var subQ7=makeQuery(id+"F0.imprint","INTERSECT",VERTEX,{"disambiguationData":[OD(0.0)],"derivedFrom":[subQ3,subQ0]});Q5=makeQuery(id+"F0.imprint","IMPRINT",FACE,{"disambiguationData":[TD([[makeQuery(id+"F0.imprint","IMPRINT",EDGE,{"disambiguationData":[TD([[subQ7,1.0]])],"derivedFrom":subQ3}),-1.0]])]});}
            var Q6;
            {var subQ3=sQuery(id+"F0.wireOp",EDGE,"E47");var subQ5=sQuery(id+"F0.wireOp",EDGE,"E55.rect.right");var subQ7=makeQuery(id+"F0.imprint","INTERSECT",VERTEX,{"derivedFrom":[subQ3,subQ5]});Q6=makeQuery(id+"F0.imprint","IMPRINT",FACE,{"disambiguationData":[TD([[makeQuery(id+"F0.imprint","IMPRINT",EDGE,{"disambiguationData":[TD([[subQ7,-1.0]])],"derivedFrom":subQ3}),-1.0]])]});}
            var Q7;
            {var subQ3=sQuery(id+"F0.wireOp",EDGE,"E52");var subQ5=sQuery(id+"F0.wireOp",EDGE,"E55.rect.right");var subQ7=makeQuery(id+"F0.imprint","INTERSECT",VERTEX,{"derivedFrom":[subQ3,subQ5]});Q7=makeQuery(id+"F0.imprint","IMPRINT",FACE,{"disambiguationData":[TD([[makeQuery(id+"F0.imprint","IMPRINT",EDGE,{"disambiguationData":[TD([[subQ7,-1.0]])],"derivedFrom":subQ3}),-1.0]])]});}
            var Q8;
            {var subQ0=sQuery(id+"F0.wireOp",EDGE,"E59.2");var subQ3=sQuery(id+"F0.wireOp",EDGE,"E44");var subQ15=makeQuery(id+"F0.imprint","INTERSECT",VERTEX,{"disambiguationData":[OD(0.0)],"derivedFrom":[subQ3,subQ0]});Q8=makeQuery(id+"F0.imprint","IMPRINT",FACE,{"disambiguationData":[TD([[makeQuery(id+"F0.imprint","IMPRINT",EDGE,{"disambiguationData":[TD([[subQ15,-1.0]])],"derivedFrom":subQ3}),-1.0]])]});}
            var Q9;
            {var subQ0=sQuery(id+"F0.wireOp",EDGE,"E59.2");var subQ3=sQuery(id+"F0.wireOp",EDGE,"E44");var subQ7=makeQuery(id+"F0.imprint","INTERSECT",VERTEX,{"disambiguationData":[OD(0.0)],"derivedFrom":[subQ3,subQ0]});Q9=makeQuery(id+"F0.imprint","IMPRINT",FACE,{"disambiguationData":[TD([[makeQuery(id+"F0.imprint","IMPRINT",EDGE,{"disambiguationData":[TD([[subQ7,1.0]])],"derivedFrom":subQ3}),-1.0]])]});}
            var Q10;
            {var subQ0=sQuery(id+"F0.wireOp",EDGE,"E56.rect.top");var subQ3=sQuery(id+"F0.wireOp",EDGE,"E53");var subQ4=makeQuery(id+"F0.imprint","INTERSECT",VERTEX,{"derivedFrom":[subQ3,subQ0]});Q10=makeQuery(id+"F0.imprint","IMPRINT",FACE,{"disambiguationData":[TD([[makeQuery(id+"F0.imprint","IMPRINT",EDGE,{"disambiguationData":[TD([[subQ4,1.0]])],"derivedFrom":subQ3}),-1.0]])]});}
            var Q11;
            {var subQ0=sQuery(id+"F0.wireOp",EDGE,"E56.rect.top");var subQ3=sQuery(id+"F0.wireOp",EDGE,"E49");var subQ4=makeQuery(id+"F0.imprint","INTERSECT",VERTEX,{"derivedFrom":[subQ3,subQ0]});Q11=makeQuery(id+"F0.imprint","IMPRINT",FACE,{"disambiguationData":[TD([[makeQuery(id+"F0.imprint","IMPRINT",EDGE,{"disambiguationData":[TD([[subQ4,-1.0]])],"derivedFrom":subQ3}),-1.0]])]});}
            var Q12;
            {var subQ1=sQuery(id+"F0.wireOp",EDGE,"E49");var subQ5=sQuery(id+"F0.wireOp",EDGE,"E59.1");var subQ6=makeQuery(id+"F0.imprint","INTERSECT",VERTEX,{"disambiguationData":[OD(0.0)],"derivedFrom":[subQ1,subQ5]});Q12=makeQuery(id+"F0.imprint","IMPRINT",FACE,{"disambiguationData":[TD([[makeQuery(id+"F0.imprint","IMPRINT",EDGE,{"disambiguationData":[TD([[subQ6,1.0]])],"derivedFrom":subQ1}),-1.0]])]});}
            var Q13;
            {var subQ0=sQuery(id+"F0.wireOp",EDGE,"E59.1");var subQ3=sQuery(id+"F0.wireOp",EDGE,"E43");var subQ13=makeQuery(id+"F0.imprint","INTERSECT",VERTEX,{"disambiguationData":[OD(0.0)],"derivedFrom":[subQ3,subQ0]});Q13=makeQuery(id+"F0.imprint","IMPRINT",FACE,{"disambiguationData":[TD([[makeQuery(id+"F0.imprint","IMPRINT",EDGE,{"disambiguationData":[TD([[subQ13,-1.0]])],"derivedFrom":subQ3}),-1.0]])]});}
            var Q14;
            {var subQ0=sQuery(id+"F0.wireOp",EDGE,"E59.1");var subQ3=sQuery(id+"F0.wireOp",EDGE,"E43");var subQ4=makeQuery(id+"F0.imprint","INTERSECT",VERTEX,{"disambiguationData":[OD(0.0)],"derivedFrom":[subQ3,subQ0]});Q14=makeQuery(id+"F0.imprint","IMPRINT",FACE,{"disambiguationData":[TD([[makeQuery(id+"F0.imprint","IMPRINT",EDGE,{"disambiguationData":[TD([[subQ4,1.0]])],"derivedFrom":subQ3}),-1.0]])]});}
            var Q15;
            {var subQ3=sQuery(id+"F0.wireOp",EDGE,"E49");var subQ5=sQuery(id+"F0.wireOp",EDGE,"E55.rect.left");var subQ7=makeQuery(id+"F0.imprint","INTERSECT",VERTEX,{"derivedFrom":[subQ3,subQ5]});Q15=makeQuery(id+"F0.imprint","IMPRINT",FACE,{"disambiguationData":[TD([[makeQuery(id+"F0.imprint","IMPRINT",EDGE,{"disambiguationData":[TD([[subQ7,-1.0]])],"derivedFrom":subQ3}),-1.0]])]});}
            var Q16;
            {var subQ0=sQuery(id+"F0.wireOp",EDGE,"E56.rect.left");var subQ3=sQuery(id+"F0.wireOp",EDGE,"E50");var subQ4=makeQuery(id+"F0.imprint","INTERSECT",VERTEX,{"derivedFrom":[subQ3,subQ0]});Q16=makeQuery(id+"F0.imprint","IMPRINT",FACE,{"disambiguationData":[TD([[makeQuery(id+"F0.imprint","IMPRINT",EDGE,{"disambiguationData":[TD([[subQ4,-1.0]])],"derivedFrom":subQ3}),-1.0]])]});}
            var Q17;
            {var subQ0=sQuery(id+"F0.wireOp",EDGE,"E56.rect.left");var subQ3=sQuery(id+"F0.wireOp",EDGE,"E46");var subQ4=makeQuery(id+"F0.imprint","INTERSECT",VERTEX,{"derivedFrom":[subQ3,subQ0]});Q17=makeQuery(id+"F0.imprint","IMPRINT",FACE,{"disambiguationData":[TD([[makeQuery(id+"F0.imprint","IMPRINT",EDGE,{"disambiguationData":[TD([[subQ4,-1.0]])],"derivedFrom":subQ3}),-1.0]])]});}
            var Q18;
            {var subQ3=sQuery(id+"F0.wireOp",EDGE,"E46");var subQ5=sQuery(id+"F0.wireOp",EDGE,"E55.rect.bottom");var subQ7=makeQuery(id+"F0.imprint","INTERSECT",VERTEX,{"derivedFrom":[subQ3,subQ5]});Q18=makeQuery(id+"F0.imprint","IMPRINT",FACE,{"disambiguationData":[TD([[makeQuery(id+"F0.imprint","IMPRINT",EDGE,{"disambiguationData":[TD([[subQ7,-1.0]])],"derivedFrom":subQ3}),-1.0]])]});}
            var Q19;
            {var subQ0=sQuery(id+"F0.wireOp",EDGE,"E59.0");var subQ3=sQuery(id+"F0.wireOp",EDGE,"E42");var subQ7=makeQuery(id+"F0.imprint","INTERSECT",VERTEX,{"disambiguationData":[OD(0.0)],"derivedFrom":[subQ3,subQ0]});Q19=makeQuery(id+"F0.imprint","IMPRINT",FACE,{"disambiguationData":[TD([[makeQuery(id+"F0.imprint","IMPRINT",EDGE,{"disambiguationData":[TD([[subQ7,-1.0]])],"derivedFrom":subQ3}),-1.0]])]});}
            var Q20;
            {var subQ0=sQuery(id+"F0.wireOp",EDGE,"E59.0");var subQ3=sQuery(id+"F0.wireOp",EDGE,"E42");var subQ7=makeQuery(id+"F0.imprint","INTERSECT",VERTEX,{"disambiguationData":[OD(0.0)],"derivedFrom":[subQ3,subQ0]});Q20=makeQuery(id+"F0.imprint","IMPRINT",FACE,{"disambiguationData":[TD([[makeQuery(id+"F0.imprint","IMPRINT",EDGE,{"disambiguationData":[TD([[subQ7,1.0]])],"derivedFrom":subQ3}),-1.0]])]});}
            var Q21;
            {var subQ3=sQuery(id+"F0.wireOp",EDGE,"E50");var subQ5=sQuery(id+"F0.wireOp",EDGE,"E55.rect.bottom");var subQ7=makeQuery(id+"F0.imprint","INTERSECT",VERTEX,{"derivedFrom":[subQ3,subQ5]});Q21=makeQuery(id+"F0.imprint","IMPRINT",FACE,{"disambiguationData":[TD([[makeQuery(id+"F0.imprint","IMPRINT",EDGE,{"disambiguationData":[TD([[subQ7,-1.0]])],"derivedFrom":subQ3}),-1.0]])]});}
            var Q22;
            {var subQ1=sQuery(id+"F0.wireOp",EDGE,"E49");var subQ5=sQuery(id+"F0.wireOp",EDGE,"E66");var subQ6=makeQuery(id+"F0.imprint","INTERSECT",VERTEX,{"derivedFrom":[subQ1,subQ5]});Q22=makeQuery(id+"F0.imprint","IMPRINT",FACE,{"disambiguationData":[TD([[makeQuery(id+"F0.imprint","IMPRINT",EDGE,{"disambiguationData":[TD([[subQ6,-1.0]])],"derivedFrom":subQ1}),-1.0]])]});}
            var Q23;
            {var subQ0=sQuery(id+"F0.wireOp",EDGE,"E62");var subQ1=sQuery(id+"F0.wireOp",EDGE,"E46");var subQ2=makeQuery(id+"F0.imprint","INTERSECT",VERTEX,{"derivedFrom":[subQ1,subQ0]});Q23=makeQuery(id+"F0.imprint","IMPRINT",FACE,{"disambiguationData":[TD([[makeQuery(id+"F0.imprint","IMPRINT",EDGE,{"disambiguationData":[TD([[subQ2,1.0]])],"derivedFrom":subQ1}),-1.0]])]});}
            var Q24;
            {var subQ0=sQuery(id+"F0.wireOp",EDGE,"E63");var subQ1=sQuery(id+"F0.wireOp",EDGE,"E46");var subQ2=makeQuery(id+"F0.imprint","INTERSECT",VERTEX,{"derivedFrom":[subQ1,subQ0]});Q24=makeQuery(id+"F0.imprint","IMPRINT",FACE,{"disambiguationData":[TD([[makeQuery(id+"F0.imprint","IMPRINT",EDGE,{"disambiguationData":[TD([[subQ2,1.0]])],"derivedFrom":subQ1}),-1.0]])]});}
            var Q25;
            {var subQ0=sQuery(id+"F0.wireOp",EDGE,"E61");var subQ1=sQuery(id+"F0.wireOp",EDGE,"E47");var subQ2=makeQuery(id+"F0.imprint","INTERSECT",VERTEX,{"derivedFrom":[subQ1,subQ0]});Q25=makeQuery(id+"F0.imprint","IMPRINT",FACE,{"disambiguationData":[TD([[makeQuery(id+"F0.imprint","IMPRINT",EDGE,{"disambiguationData":[TD([[subQ2,-1.0]])],"derivedFrom":subQ1}),-1.0]])]});}
            var Q26;
            {var subQ0=sQuery(id+"F0.wireOp",EDGE,"E60");var subQ1=sQuery(id+"F0.wireOp",EDGE,"E47");var subQ2=makeQuery(id+"F0.imprint","INTERSECT",VERTEX,{"derivedFrom":[subQ1,subQ0]});Q26=makeQuery(id+"F0.imprint","IMPRINT",FACE,{"disambiguationData":[TD([[makeQuery(id+"F0.imprint","IMPRINT",EDGE,{"disambiguationData":[TD([[subQ2,-1.0]])],"derivedFrom":subQ1}),-1.0]])]});}
            var Q27;
            {var subQ1=sQuery(id+"F0.wireOp",EDGE,"E48");var subQ5=sQuery(id+"F0.wireOp",EDGE,"E59.2");var subQ6=makeQuery(id+"F0.imprint","INTERSECT",VERTEX,{"disambiguationData":[OD(0.0)],"derivedFrom":[subQ1,subQ5]});Q27=makeQuery(id+"F0.imprint","IMPRINT",FACE,{"disambiguationData":[TD([[makeQuery(id+"F0.imprint","IMPRINT",EDGE,{"disambiguationData":[TD([[subQ6,-1.0]])],"derivedFrom":subQ1}),-1.0]])]});}
            var Q28;
            {var subQ3=sQuery(id+"F0.wireOp",EDGE,"E47");var subQ5=sQuery(id+"F0.wireOp",EDGE,"E59.3");var subQ6=makeQuery(id+"F0.imprint","INTERSECT",VERTEX,{"disambiguationData":[OD(1.0)],"derivedFrom":[subQ3,subQ5]});Q28=makeQuery(id+"F0.imprint","IMPRINT",FACE,{"disambiguationData":[TD([[makeQuery(id+"F0.imprint","IMPRINT",EDGE,{"disambiguationData":[TD([[subQ6,-1.0]])],"derivedFrom":subQ3}),-1.0]])]});}
            var Q29;
            {var subQ0=sQuery(id+"F0.wireOp",EDGE,"E59.3");var subQ1=sQuery(id+"F0.wireOp",EDGE,"E47");var subQ2=makeQuery(id+"F0.imprint","INTERSECT",VERTEX,{"disambiguationData":[OD(0.0)],"derivedFrom":[subQ1,subQ0]});Q29=makeQuery(id+"F0.imprint","IMPRINT",FACE,{"disambiguationData":[TD([[makeQuery(id+"F0.imprint","IMPRINT",EDGE,{"disambiguationData":[TD([[subQ2,-1.0]])],"derivedFrom":subQ1}),-1.0]])]});}
            var Q30;
            {var subQ0=sQuery(id+"F0.wireOp",EDGE,"E59.3");var subQ1=sQuery(id+"F0.wireOp",EDGE,"E47");var subQ2=makeQuery(id+"F0.imprint","INTERSECT",VERTEX,{"disambiguationData":[OD(0.0)],"derivedFrom":[subQ1,subQ0]});Q30=makeQuery(id+"F0.imprint","IMPRINT",FACE,{"disambiguationData":[TD([[makeQuery(id+"F0.imprint","IMPRINT",EDGE,{"disambiguationData":[TD([[subQ2,1.0]])],"derivedFrom":subQ1}),-1.0]])]});}
            var Q31;
            {var subQ0=sQuery(id+"F0.wireOp",EDGE,"E62");var subQ1=sQuery(id+"F0.wireOp",EDGE,"E46");var subQ2=makeQuery(id+"F0.imprint","INTERSECT",VERTEX,{"derivedFrom":[subQ1,subQ0]});Q31=makeQuery(id+"F0.imprint","IMPRINT",FACE,{"disambiguationData":[TD([[makeQuery(id+"F0.imprint","IMPRINT",EDGE,{"disambiguationData":[TD([[subQ2,-1.0]])],"derivedFrom":subQ1}),-1.0]])]});}
            var Q32;
            {var subQ0=sQuery(id+"F0.wireOp",EDGE,"E59.0");var subQ1=sQuery(id+"F0.wireOp",EDGE,"E46");var subQ2=makeQuery(id+"F0.imprint","INTERSECT",VERTEX,{"disambiguationData":[OD(0.0)],"derivedFrom":[subQ1,subQ0]});Q32=makeQuery(id+"F0.imprint","IMPRINT",FACE,{"disambiguationData":[TD([[makeQuery(id+"F0.imprint","IMPRINT",EDGE,{"disambiguationData":[TD([[subQ2,-1.0]])],"derivedFrom":subQ1}),-1.0]])]});}
            var Q33;
            {var subQ1=sQuery(id+"F0.wireOp",EDGE,"E46");var subQ5=sQuery(id+"F0.wireOp",EDGE,"E55.rect.left");var subQ7=makeQuery(id+"F0.imprint","INTERSECT",VERTEX,{"derivedFrom":[subQ1,subQ5]});Q33=makeQuery(id+"F0.imprint","IMPRINT",FACE,{"disambiguationData":[TD([[makeQuery(id+"F0.imprint","IMPRINT",EDGE,{"disambiguationData":[TD([[subQ7,-1.0]])],"derivedFrom":subQ1}),-1.0]])]});}
            var Q34;
            {var subQ1=sQuery(id+"F0.wireOp",EDGE,"E49");var subQ5=sQuery(id+"F0.wireOp",EDGE,"E55.rect.left");var subQ7=makeQuery(id+"F0.imprint","INTERSECT",VERTEX,{"derivedFrom":[subQ1,subQ5]});Q34=makeQuery(id+"F0.imprint","IMPRINT",FACE,{"disambiguationData":[TD([[makeQuery(id+"F0.imprint","IMPRINT",EDGE,{"disambiguationData":[TD([[subQ7,1.0]])],"derivedFrom":subQ1}),-1.0]])]});}
            var Q35;
            {var subQ1=sQuery(id+"F0.wireOp",EDGE,"E49");var subQ5=sQuery(id+"F0.wireOp",EDGE,"E59.1");var subQ6=makeQuery(id+"F0.imprint","INTERSECT",VERTEX,{"disambiguationData":[OD(1.0)],"derivedFrom":[subQ1,subQ5]});Q35=makeQuery(id+"F0.imprint","IMPRINT",FACE,{"disambiguationData":[TD([[makeQuery(id+"F0.imprint","IMPRINT",EDGE,{"disambiguationData":[TD([[subQ6,-1.0]])],"derivedFrom":subQ1}),-1.0]])]});}
            var Q36;
            {var subQ1=sQuery(id+"F0.wireOp",EDGE,"E49");var subQ5=sQuery(id+"F0.wireOp",EDGE,"E55.rect.top");var subQ7=makeQuery(id+"F0.imprint","INTERSECT",VERTEX,{"derivedFrom":[subQ1,subQ5]});Q36=makeQuery(id+"F0.imprint","IMPRINT",FACE,{"disambiguationData":[TD([[makeQuery(id+"F0.imprint","IMPRINT",EDGE,{"disambiguationData":[TD([[subQ7,-1.0]])],"derivedFrom":subQ1}),-1.0]])]});}
            var Q37;
            {var subQ0=sQuery(id+"F0.wireOp",EDGE,"E65");var subQ1=sQuery(id+"F0.wireOp",EDGE,"E48");var subQ2=makeQuery(id+"F0.imprint","INTERSECT",VERTEX,{"derivedFrom":[subQ1,subQ0]});Q37=makeQuery(id+"F0.imprint","IMPRINT",FACE,{"disambiguationData":[TD([[makeQuery(id+"F0.imprint","IMPRINT",EDGE,{"disambiguationData":[TD([[subQ2,-1.0]])],"derivedFrom":subQ1}),-1.0]])]});}
            var Q38;
            {var subQ0=sQuery(id+"F0.wireOp",EDGE,"E59.2");var subQ1=sQuery(id+"F0.wireOp",EDGE,"E48");var subQ2=makeQuery(id+"F0.imprint","INTERSECT",VERTEX,{"disambiguationData":[OD(1.0)],"derivedFrom":[subQ1,subQ0]});Q38=makeQuery(id+"F0.imprint","IMPRINT",FACE,{"disambiguationData":[TD([[makeQuery(id+"F0.imprint","IMPRINT",EDGE,{"disambiguationData":[TD([[subQ2,-1.0]])],"derivedFrom":subQ1}),-1.0]])]});}
            var Q39;
            {var subQ1=sQuery(id+"F0.wireOp",EDGE,"E48");var subQ5=sQuery(id+"F0.wireOp",EDGE,"E55.rect.right");var subQ7=makeQuery(id+"F0.imprint","INTERSECT",VERTEX,{"derivedFrom":[subQ1,subQ5]});Q39=makeQuery(id+"F0.imprint","IMPRINT",FACE,{"disambiguationData":[TD([[makeQuery(id+"F0.imprint","IMPRINT",EDGE,{"disambiguationData":[TD([[subQ7,-1.0]])],"derivedFrom":subQ1}),-1.0]])]});}
            extrude(context, id + "F10", {"entities" : qUnion([Q0, Q1, Q2, Q3, Q4, Q5, Q6, Q7, Q8, Q9, Q10, Q11, Q12, Q13, Q14, Q15, Q16, Q17, Q18, Q19, Q20, Q21, Q22, Q23, Q24, Q25, Q26, Q27, Q28, Q29, Q30, Q31, Q32, Q33, Q34, Q35, Q36, Q37, Q38, Q39]), "depth" : 2 * mm});
        }
        {
            var Q0;
            Q0=makeQuery(id+"F10.opExtrude","SWEPT_EDGE",EDGE,{"disambiguationData":[OSD([sQuery(id+"F0.wireOp",EDGE,"E52"),sQuery(id+"F0.wireOp",EDGE,"E55.rect.bottom")])]});
            var Q1;
            Q1=makeQuery(id+"F10.opExtrude","SWEPT_EDGE",EDGE,{"disambiguationData":[OSD([sQuery(id+"F0.wireOp",EDGE,"E53"),sQuery(id+"F0.wireOp",EDGE,"E56.rect.top")])]});
            var Q2;
            Q2=makeQuery(id+"F10.opExtrude","SWEPT_EDGE",EDGE,{"disambiguationData":[OSD([sQuery(id+"F0.wireOp",EDGE,"E46"),sQuery(id+"F0.wireOp",EDGE,"E55.rect.bottom")])]});
            var Q3;
            Q3=makeQuery(id+"F10.opExtrude","SWEPT_EDGE",EDGE,{"disambiguationData":[OSD([sQuery(id+"F0.wireOp",EDGE,"E49"),sQuery(id+"F0.wireOp",EDGE,"E56.rect.top")])]});
            var Q4;
            Q4=makeQuery(id+"F10.opExtrude","SWEPT_EDGE",EDGE,{"disambiguationData":[OSD([sQuery(id+"F0.wireOp",EDGE,"E50"),sQuery(id+"F0.wireOp",EDGE,"E55.rect.bottom")])]});
            var Q5;
            Q5=makeQuery(id+"F10.opExtrude","SWEPT_EDGE",EDGE,{"disambiguationData":[OSD([sQuery(id+"F0.wireOp",EDGE,"E47"),sQuery(id+"F0.wireOp",EDGE,"E55.rect.bottom")])]});
            var Q6;
            Q6=makeQuery(id+"F10.opExtrude","SWEPT_EDGE",EDGE,{"disambiguationData":[OSD([sQuery(id+"F0.wireOp",EDGE,"E48"),sQuery(id+"F0.wireOp",EDGE,"E56.rect.top")])]});
            var Q7;
            Q7=makeQuery(id+"F10.opExtrude","SWEPT_EDGE",EDGE,{"disambiguationData":[OSD([sQuery(id+"F0.wireOp",EDGE,"E54"),sQuery(id+"F0.wireOp",EDGE,"E56.rect.top")])]});
            var Q8;
            Q8=makeQuery(id+"F10.opExtrude","SWEPT_EDGE",EDGE,{"disambiguationData":[OSD([sQuery(id+"F0.wireOp",EDGE,"E55.rect.top"),sQuery(id+"F0.wireOp",EDGE,"E55.rect.right"),sQuery(id+"F0.wireOp",EDGE,"E64")])]});
            var Q9;
            Q9=makeQuery(id+"F10.opExtrude","SWEPT_EDGE",EDGE,{"disambiguationData":[OSD([sQuery(id+"F0.wireOp",EDGE,"E55.rect.top"),sQuery(id+"F0.wireOp",EDGE,"E55.rect.left"),sQuery(id+"F0.wireOp",EDGE,"E67")])]});
            var Q10;
            Q10=makeQuery(id+"F10.opExtrude","SWEPT_EDGE",EDGE,{"disambiguationData":[OSD([sQuery(id+"F0.wireOp",EDGE,"E55.rect.bottom"),sQuery(id+"F0.wireOp",EDGE,"E55.rect.left"),sQuery(id+"F0.wireOp",EDGE,"E63")])]});
            var Q11;
            Q11=makeQuery(id+"F10.opExtrude","SWEPT_EDGE",EDGE,{"disambiguationData":[OSD([sQuery(id+"F0.wireOp",EDGE,"E55.rect.bottom"),sQuery(id+"F0.wireOp",EDGE,"E55.rect.right"),sQuery(id+"F0.wireOp",EDGE,"E60")])]});
            var Q12;
            Q12=makeQuery(id+"F10.opExtrude","SWEPT_EDGE",EDGE,{"disambiguationData":[OSD([sQuery(id+"F0.wireOp",EDGE,"E46"),sQuery(id+"F0.wireOp",EDGE,"E55.rect.left")])]});
            var Q13;
            Q13=makeQuery(id+"F10.opExtrude","SWEPT_EDGE",EDGE,{"disambiguationData":[OSD([sQuery(id+"F0.wireOp",EDGE,"E47"),sQuery(id+"F0.wireOp",EDGE,"E55.rect.right")])]});
            var Q14;
            Q14=makeQuery(id+"F10.opExtrude","SWEPT_EDGE",EDGE,{"disambiguationData":[OSD([sQuery(id+"F0.wireOp",EDGE,"E56.rect.bottom"),sQuery(id+"F0.wireOp",EDGE,"E56.rect.right")])]});
            var Q15;
            Q15=makeQuery(id+"F10.opExtrude","SWEPT_EDGE",EDGE,{"disambiguationData":[OSD([sQuery(id+"F0.wireOp",EDGE,"E56.rect.bottom"),sQuery(id+"F0.wireOp",EDGE,"E56.rect.left")])]});
            fillet(context, id + "F11", {"entities" : qUnion([Q0, Q1, Q2, Q3, Q4, Q5, Q6, Q7, Q8, Q9, Q10, Q11, Q12, Q13, Q14, Q15]), "radius" : 1.5 * mm, "tangentPropagation" : true, "allowEdgeOverflow" : false});
        }
        {
            var Q0;
            {var subQ0=sQuery(id+"F0.wireOp",EDGE,"E24");var subQ1=sQuery(id+"F0.wireOp",EDGE,"E38");var subQ18=sQuery(id+"F0.wireOp",EDGE,"E5");Q0=makeQuery(id+"F8.boolean.opBoolean","SPLIT",EDGE,{"disambiguationData":[TD([makeQuery(id+"F6.opExtrude","CAP_FACE",FACE,{"disambiguationData":[OSD([subQ18])],"isStart":true})])],"derivedFrom":makeQuery(id+"F8.opExtrude","SWEPT_EDGE",EDGE,{"disambiguationData":[OSD([subQ0,subQ1])]})});}
            var Q1;
            {var subQ0=sQuery(id+"F0.wireOp",EDGE,"E26");var subQ1=sQuery(id+"F0.wireOp",EDGE,"E38");var subQ18=sQuery(id+"F0.wireOp",EDGE,"E5");Q1=makeQuery(id+"F8.boolean.opBoolean","SPLIT",EDGE,{"disambiguationData":[TD([makeQuery(id+"F6.opExtrude","CAP_FACE",FACE,{"disambiguationData":[OSD([subQ18])],"isStart":true})])],"derivedFrom":makeQuery(id+"F8.opExtrude","SWEPT_EDGE",EDGE,{"disambiguationData":[OSD([subQ0,subQ1])]})});}
            var Q2;
            {var subQ0=sQuery(id+"F0.wireOp",EDGE,"E28");var subQ1=sQuery(id+"F0.wireOp",EDGE,"E40");var subQ18=sQuery(id+"F0.wireOp",EDGE,"E5");Q2=makeQuery(id+"F8.boolean.opBoolean","SPLIT",EDGE,{"disambiguationData":[TD([makeQuery(id+"F6.opExtrude","CAP_FACE",FACE,{"disambiguationData":[OSD([subQ18])],"isStart":true})])],"derivedFrom":makeQuery(id+"F8.opExtrude","SWEPT_EDGE",EDGE,{"disambiguationData":[OSD([subQ0,subQ1])]})});}
            var Q3;
            {var subQ0=sQuery(id+"F0.wireOp",EDGE,"E27");var subQ1=sQuery(id+"F0.wireOp",EDGE,"E40");var subQ18=sQuery(id+"F0.wireOp",EDGE,"E5");Q3=makeQuery(id+"F8.boolean.opBoolean","SPLIT",EDGE,{"disambiguationData":[TD([makeQuery(id+"F6.opExtrude","CAP_FACE",FACE,{"disambiguationData":[OSD([subQ18])],"isStart":true})])],"derivedFrom":makeQuery(id+"F8.opExtrude","SWEPT_EDGE",EDGE,{"disambiguationData":[OSD([subQ0,subQ1])]})});}
            var Q4;
            {var subQ0=sQuery(id+"F0.wireOp",EDGE,"E30");var subQ1=sQuery(id+"F0.wireOp",EDGE,"E33");var subQ19=sQuery(id+"F0.wireOp",EDGE,"E5");Q4=makeQuery(id+"F8.boolean.opBoolean","SPLIT",EDGE,{"disambiguationData":[TD([makeQuery(id+"F6.opExtrude","CAP_FACE",FACE,{"disambiguationData":[OSD([subQ19])],"isStart":true})])],"derivedFrom":makeQuery(id+"F8.opExtrude","SWEPT_EDGE",EDGE,{"disambiguationData":[OSD([subQ0,subQ1])]})});}
            var Q5;
            {var subQ0=sQuery(id+"F0.wireOp",EDGE,"E29");var subQ1=sQuery(id+"F0.wireOp",EDGE,"E33");var subQ18=sQuery(id+"F0.wireOp",EDGE,"E5");Q5=makeQuery(id+"F8.boolean.opBoolean","SPLIT",EDGE,{"disambiguationData":[TD([makeQuery(id+"F6.opExtrude","CAP_FACE",FACE,{"disambiguationData":[OSD([subQ18])],"isStart":true})])],"derivedFrom":makeQuery(id+"F8.opExtrude","SWEPT_EDGE",EDGE,{"disambiguationData":[OSD([subQ0,subQ1])]})});}
            var Q6;
            {var subQ0=sQuery(id+"F0.wireOp",EDGE,"E23");var subQ1=sQuery(id+"F0.wireOp",EDGE,"E36");var subQ18=sQuery(id+"F0.wireOp",EDGE,"E5");Q6=makeQuery(id+"F8.boolean.opBoolean","SPLIT",EDGE,{"disambiguationData":[TD([makeQuery(id+"F6.opExtrude","CAP_FACE",FACE,{"disambiguationData":[OSD([subQ18])],"isStart":true})])],"derivedFrom":makeQuery(id+"F8.opExtrude","SWEPT_EDGE",EDGE,{"disambiguationData":[OSD([subQ0,subQ1])]})});}
            var Q7;
            {var subQ0=sQuery(id+"F0.wireOp",EDGE,"E31");var subQ1=sQuery(id+"F0.wireOp",EDGE,"E36");var subQ19=sQuery(id+"F0.wireOp",EDGE,"E5");Q7=makeQuery(id+"F8.boolean.opBoolean","SPLIT",EDGE,{"disambiguationData":[TD([makeQuery(id+"F6.opExtrude","CAP_FACE",FACE,{"disambiguationData":[OSD([subQ19])],"isStart":true})])],"derivedFrom":makeQuery(id+"F8.opExtrude","SWEPT_EDGE",EDGE,{"disambiguationData":[OSD([subQ0,subQ1])]})});}
            fillet(context, id + "F12", {"entities" : qUnion([Q0, Q1, Q2, Q3, Q4, Q5, Q6, Q7]), "radius" : 4 * mm, "tangentPropagation" : true, "allowEdgeOverflow" : false});
        }
    });
